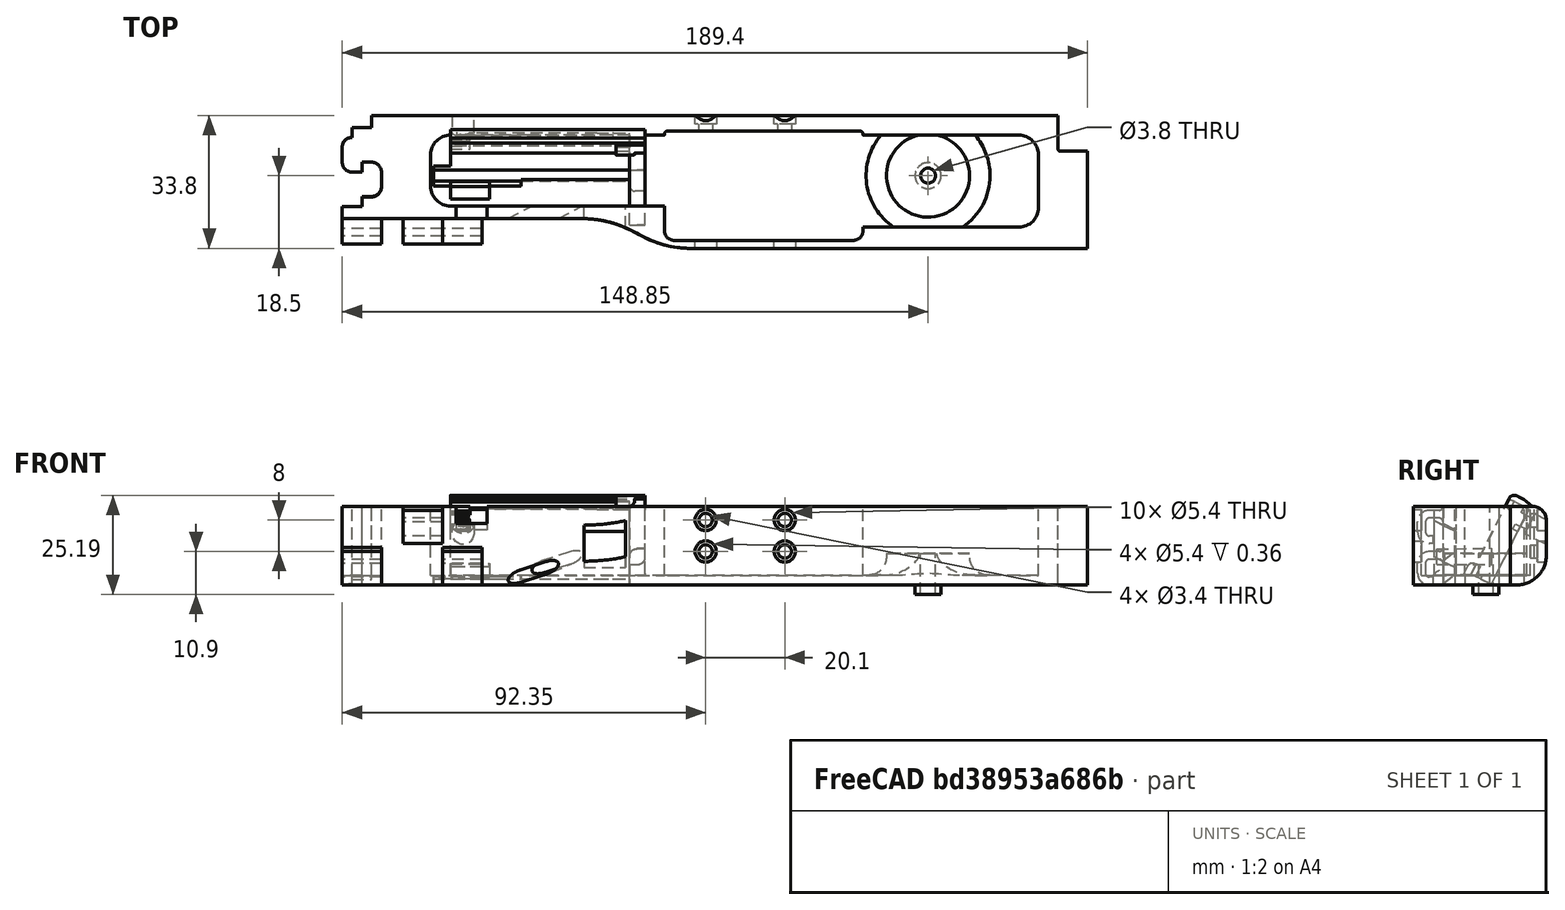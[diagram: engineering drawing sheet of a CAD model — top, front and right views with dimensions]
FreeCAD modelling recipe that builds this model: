
FCSTD DOCUMENT  (FreeCAD 0.19R0.19.2)
Label: v0_9992
License: All rights reserved
LicenseURL: http://en.wikipedia.org/wiki/All_rights_reserved
objects: Sketcher::SketchObject×44, Part::Extrusion×35, Part::MultiFuse×20, Part::Cut×15, Part::Box×14, Part::Fillet×13, App::MeasureDistance×5, Part::Cylinder×4, Part::Revolution×1, Mesh::Feature×1
note: 146 computed .brp shape members not serialized (recipe doc carries the construction recipe); baked Part::Feature solids carry a one-line shape summary decoded from their .brp

FEATURE [Sketcher::SketchObject] Sketch
  FullyConstrained = true
  sketch-geometry (36):
    g0: LineSegment StartX=0 StartY=0 StartZ=0 EndX=154.4 EndY=0 EndZ=0
    g1: LineSegment StartX=154.4 StartY=0 StartZ=0 EndX=154.4 EndY=-7.6 EndZ=0
    g2: LineSegment StartX=32.5209 StartY=-26.2 StartZ=0 EndX=-7.5 EndY=-26.2 EndZ=0
    g3-g7: Circle x5 (B-spline internal-alignment scaffolding for g8; pole/knot coordinates omitted)
    g8: BSplineCurve PolesCount=5 KnotsCount=3 Degree=3 IsPeriodic=0
    g9: GeomPoint X=61.85 Y=-33.8 Z=0
    g10: GeomPoint X=47.185 Y=-29.9 Z=0
    g11: GeomPoint X=32.5209 Y=-26.2 Z=0
    g12: Circle CenterX=121.35 CenterY=-14.3 CenterZ=0 NormalX=0 NormalY=0 NormalZ=1 AngleXU=0 Radius=3.25
    g13: LineSegment StartX=-7.5 StartY=-26.2 StartZ=0 EndX=-27.5 EndY=-26.2 EndZ=0
    g14: LineSegment StartX=-20 StartY=0 StartZ=0 EndX=0 EndY=0 EndZ=0
    g15: LineSegment StartX=-25 StartY=-3.1 StartZ=0 EndX=-20 EndY=-3.1 EndZ=0
    g16: LineSegment StartX=-25 StartY=-3.1 StartZ=0 EndX=-25 EndY=-5.6 EndZ=0
    g17: LineSegment StartX=-27.5 StartY=-8.1 StartZ=0 EndX=-27.5 EndY=-11.85 EndZ=0
    g18: ArcOfCircle CenterX=-25 CenterY=-8.1 CenterZ=0 NormalX=0 NormalY=0 NormalZ=1 AngleXU=0 Radius=2.5 StartAngle=1.5708 EndAngle=3.14159
    g19: LineSegment StartX=-25 StartY=-14.35 StartZ=0 EndX=-22.5 EndY=-14.35 EndZ=0
    g20: ArcOfCircle CenterX=-25 CenterY=-11.85 CenterZ=0 NormalX=0 NormalY=0 NormalZ=1 AngleXU=0 Radius=2.5 StartAngle=3.14159 EndAngle=4.71239
    g21: LineSegment StartX=-22.5 StartY=-14.35 StartZ=0 EndX=-22.5 EndY=-11.85 EndZ=0
    g22: LineSegment StartX=-22.5 StartY=-11.85 StartZ=0 EndX=-20 EndY=-11.85 EndZ=0
    g23: ArcOfCircle CenterX=-20 CenterY=-14.35 CenterZ=0 NormalX=0 NormalY=0 NormalZ=1 AngleXU=0 Radius=2.5 StartAngle=8e-16 EndAngle=1.5708
    g24: LineSegment StartX=-17.5 StartY=-14.35 StartZ=0 EndX=-17.5 EndY=-18.1 EndZ=0
    g25: ArcOfCircle CenterX=-20 CenterY=-18.1 CenterZ=0 NormalX=0 NormalY=0 NormalZ=1 AngleXU=0 Radius=2.5 StartAngle=4.71239 EndAngle=6.28319
    g26: LineSegment StartX=-22.5 StartY=-20.6 StartZ=0 EndX=-20 EndY=-20.6 EndZ=0
    g27: LineSegment StartX=-22.5 StartY=-20.6 StartZ=0 EndX=-22.5 EndY=-23.1 EndZ=0
    g28: LineSegment StartX=-27.5 StartY=-23.1 StartZ=0 EndX=-22.5 EndY=-23.1 EndZ=0
    g29: LineSegment StartX=-20 StartY=-3.1 StartZ=0 EndX=-20 EndY=0 EndZ=0
    g30: LineSegment StartX=-27.5 StartY=-23.1 StartZ=0 EndX=-27.5 EndY=-26.2 EndZ=0
    g31: LineSegment StartX=154.4 StartY=-7.6 StartZ=0 EndX=154.4 EndY=-8.6 EndZ=0
    g32: ArcOfCircle CenterX=154.9 CenterY=-8.6 CenterZ=0 NormalX=0 NormalY=0 NormalZ=1 AngleXU=0 Radius=0.5 StartAngle=3.14159 EndAngle=4.71239
    g33: LineSegment StartX=154.9 StartY=-9.1 StartZ=0 EndX=161.9 EndY=-9.1 EndZ=0
    g34: LineSegment StartX=161.9 StartY=-9.1 StartZ=0 EndX=161.9 EndY=-33.8 EndZ=0
    g35: LineSegment StartX=161.9 StartY=-33.8 StartZ=0 EndX=61.85 EndY=-33.8 EndZ=0
  constraints (72):
    c: PointOnObject(g0,g-2)
    c: Horizontal(g0)
    c: Distance(g0) = 154.4
    c: DistanceY(g-1,g0) = 0
    c: Vertical(g1)
    c: Distance(g1) = 7.6
    c: Coincident(g1,g0)
    c: Horizontal(g2)
    c: Block(g2)
    c: Weight(g3) = 1
    c: Coincident(g8,g2)
    c: InternalAlignment(g3-g7 -> g8) x5
    c: InternalAlignment(g9,g8)
    c: InternalAlignment(g10,g8)
    c: InternalAlignment(g11,g8)
    c: Block(g12)
    c: Coincident(g13,g2)
    c: Horizontal(g13)
    c: Distance(g13) = 20
    c: Horizontal(g14)
    c: Distance(g14) = 20
    c: Coincident(g14,g0)
    c: Horizontal(g15)
    c: Vertical(g16)
    c: Coincident(g16,g15)
    c: Vertical(g17)
    c: Coincident(g18,g16)
    c: Block(g18)
    c: Coincident(g17,g18)
    c: Horizontal(g19)
    c: Coincident(g20,g17)
    c: Block(g20)
    c: Block(g19)
    c: Vertical(g21)
    c: Coincident(g21,g19)
    c: Horizontal(g22)
    c: Coincident(g22,g21)
    c: Coincident(g23,g22)
    c: Vertical(g24)
    c: Block(g23)
    c: Coincident(g24,g23)
    c: Coincident(g25,g24)
    c: Block(g25)
    c: Horizontal(g26)
    c: Coincident(g26,g25)
    c: Vertical(g27)
    c: Coincident(g27,g26)
    c: Horizontal(g28)
    c: Coincident(g28,g27)
    c: Block(g15)
    c: Block(g28)
    c: Coincident(g29,g15)
    c: Coincident(g29,g14)
    c: Vertical(g29)
    c: Coincident(g30,g28)
    c: Coincident(g30,g13)
    c: Vertical(g30)
    c: Vertical(g31)
    c: Distance(g31) = 1
    c: Coincident(g31,g1)
    c: Coincident(g32,g31)
    c: Block(g32)
    c: Coincident(g33,g32)
    c: Horizontal(g33)
    c: Coincident(g34,g33)
    c: Vertical(g34)
    c: Block(g34)
    c: Coincident(g35,g34)
    c: Horizontal(g35)
    c: Block(g35)
    c: Coincident(g8,g35)
    c: Block(g8)
FEATURE [Part::Extrusion] Extrude  label="mainBodyBaseExtrude"
  Base = -> Sketch
  Dir = (0,0,1)
  DirMode = 2
  FaceMakerClass = Part::FaceMakerBullseye
  LengthFwd = 2.4
  LengthRev = 0
  Solid = true
  Symmetric = false
FEATURE [Sketcher::SketchObject] Sketch001
  FullyConstrained = true
  sketch-geometry (75):
    g0: ArcOfCircle CenterX=144.4 CenterY=-10 CenterZ=0 NormalX=0 NormalY=0 NormalZ=1 AngleXU=0 Radius=5 StartAngle=4.345e-13 EndAngle=1.5708
    g1: LineSegment StartX=32.5209 StartY=-26.2 StartZ=0 EndX=-7.49911 EndY=-26.2 EndZ=0
    g2: LineSegment StartX=0 StartY=0 StartZ=0 EndX=154.4 EndY=0 EndZ=0
    g3-g7: Circle x5 (B-spline internal-alignment scaffolding for g8; pole/knot coordinates omitted)
    g8: BSplineCurve PolesCount=5 KnotsCount=3 Degree=3 IsPeriodic=0
    g9: GeomPoint X=61.85 Y=-33.8 Z=0
    g10: GeomPoint X=47.1857 Y=-29.9 Z=0
    g11: GeomPoint X=32.5209 Y=-26.2 Z=0
    g12: LineSegment StartX=154.4 StartY=0 StartZ=0 EndX=154.4 EndY=-7.6 EndZ=0
    g13: LineSegment StartX=20 StartY=-5 StartZ=0 EndX=54.35 EndY=-5 EndZ=0
    g14: LineSegment StartX=104.85 StartY=-5 StartZ=0 EndX=144.4 EndY=-5 EndZ=0
    g15: LineSegment StartX=54.35 StartY=-23 StartZ=0 EndX=20 EndY=-23 EndZ=0
    g16: LineSegment StartX=-27.4991 StartY=-26.2 StartZ=0 EndX=-7.49911 EndY=-26.2 EndZ=0
    g17: LineSegment StartX=-20 StartY=0 StartZ=0 EndX=0 EndY=0 EndZ=0
    g18: LineSegment StartX=-27.4991 StartY=-23.2 StartZ=0 EndX=-22.5 EndY=-23.2 EndZ=0
    g19: LineSegment StartX=-22.5 StartY=-20.7 StartZ=0 EndX=-22.5 EndY=-23.2 EndZ=0
    g20: LineSegment StartX=-22.5 StartY=-20.7 StartZ=0 EndX=-20 EndY=-20.7 EndZ=0
    g21: ArcOfCircle CenterX=-20 CenterY=-18.2 CenterZ=0 NormalX=0 NormalY=0 NormalZ=1 AngleXU=0 Radius=2.5 StartAngle=4.71239 EndAngle=6.28319
    g22: LineSegment StartX=-17.5 StartY=-14.4 StartZ=0 EndX=-17.5 EndY=-18.2 EndZ=0
    g23: ArcOfCircle CenterX=-20 CenterY=-14.4 CenterZ=0 NormalX=0 NormalY=0 NormalZ=1 AngleXU=0 Radius=2.5 StartAngle=9e-16 EndAngle=1.5708
    g24: LineSegment StartX=-22.5 StartY=-11.9 StartZ=0 EndX=-20 EndY=-11.9 EndZ=0
    g25: LineSegment StartX=-22.5 StartY=-14.4 StartZ=0 EndX=-22.5 EndY=-11.9 EndZ=0
    g26: LineSegment StartX=-25 StartY=-14.4 StartZ=0 EndX=-22.5 EndY=-14.4 EndZ=0
    g27: ArcOfCircle CenterX=-25 CenterY=-11.9 CenterZ=0 NormalX=0 NormalY=0 NormalZ=1 AngleXU=0 Radius=2.5 StartAngle=3.14159 EndAngle=4.71239
    g28: LineSegment StartX=-27.5 StartY=-8.1 StartZ=0 EndX=-27.5 EndY=-11.9 EndZ=0
    g29: ArcOfCircle CenterX=-25 CenterY=-8.1 CenterZ=0 NormalX=0 NormalY=0 NormalZ=1 AngleXU=0 Radius=2.5 StartAngle=1.5708 EndAngle=3.14159
    g30: LineSegment StartX=-25 StartY=-3.1 StartZ=0 EndX=-25 EndY=-5.6 EndZ=0
    g31: LineSegment StartX=-20 StartY=-3.1 StartZ=0 EndX=-25 EndY=-3.1 EndZ=0
    g32: LineSegment StartX=-20 StartY=0 StartZ=0 EndX=-20 EndY=-3.1 EndZ=0
    g33: LineSegment StartX=-27.4991 StartY=-26.2 StartZ=0 EndX=-27.4991 EndY=-23.2 EndZ=0
    g34: LineSegment StartX=4.09e-14 StartY=-5 StartZ=0 EndX=20 EndY=-5 EndZ=0
    g35: ArcOfCircle CenterX=7.1e-15 CenterY=-18 CenterZ=0 NormalX=0 NormalY=0 NormalZ=1 AngleXU=0 Radius=5 StartAngle=3.14159 EndAngle=4.71239
    g36: ArcOfCircle CenterX=4.26e-14 CenterY=-10 CenterZ=0 NormalX=0 NormalY=0 NormalZ=1 AngleXU=0 Radius=5 StartAngle=1.5708 EndAngle=3.14159
    g37: LineSegment StartX=-5 StartY=-18 StartZ=0 EndX=-5 EndY=-10 EndZ=0
    g38: LineSegment StartX=6.2e-15 StartY=-23 StartZ=0 EndX=20 EndY=-23 EndZ=0
    g39: LineSegment StartX=154.4 StartY=-7.6 StartZ=0 EndX=154.4 EndY=-8.6 EndZ=0
    g40: LineSegment StartX=154.9 StartY=-9.1 StartZ=0 EndX=161.9 EndY=-9.1 EndZ=0
    g41: ArcOfCircle CenterX=154.9 CenterY=-8.6 CenterZ=0 NormalX=0 NormalY=0 NormalZ=1 AngleXU=0 Radius=0.5 StartAngle=3.14159 EndAngle=4.71299
    g42: LineSegment StartX=104.85 StartY=-28.3916 StartZ=0 EndX=144.408 EndY=-28.3916 EndZ=0
    g43: LineSegment StartX=149.4 StartY=-10 StartZ=0 EndX=149.4 EndY=-23.4 EndZ=0
    g44: ArcOfCircle CenterX=144.408 CenterY=-23.4 CenterZ=0 NormalX=0 NormalY=0 NormalZ=1 AngleXU=0 Radius=4.99164 StartAngle=4.71239 EndAngle=6.28319
    g45: LineSegment StartX=104.85 StartY=-28.3916 StartZ=0 EndX=104.85 EndY=-28.7833 EndZ=0
    g46: LineSegment StartX=54.35 StartY=-28.7916 StartZ=0 EndX=54.35 EndY=-23 EndZ=0
    g47: LineSegment StartX=161.9 StartY=-33.8 StartZ=0 EndX=161.9 EndY=-9.1 EndZ=0
    g48: LineSegment StartX=61.85 StartY=-33.8 StartZ=0 EndX=161.9 EndY=-33.8 EndZ=0
    g49: Circle CenterX=54.35 CenterY=-28.7916 CenterZ=0 NormalX=0 NormalY=0 NormalZ=1 AngleXU=0 Radius=1
    g50: Circle CenterX=54.35 CenterY=-31.7916 CenterZ=0 NormalX=0 NormalY=0 NormalZ=1 AngleXU=0 Radius=1
    g51: Circle CenterX=57.35 CenterY=-31.7916 CenterZ=0 NormalX=0 NormalY=0 NormalZ=1 AngleXU=0 Radius=1
    g52: BSplineCurve PolesCount=3 KnotsCount=2 Degree=2 IsPeriodic=0
    g53: GeomPoint X=54.35 Y=-28.7916 Z=0
    g54: GeomPoint X=57.35 Y=-31.7916 Z=0
    g55: Circle CenterX=104.85 CenterY=-28.7833 CenterZ=0 NormalX=0 NormalY=0 NormalZ=1 AngleXU=0 Radius=1
    g56: Circle CenterX=104.85 CenterY=-31.7916 CenterZ=0 NormalX=0 NormalY=0 NormalZ=1 AngleXU=0 Radius=1
    g57: Circle CenterX=101.85 CenterY=-31.7916 CenterZ=0 NormalX=0 NormalY=0 NormalZ=1 AngleXU=0 Radius=1
    g58: BSplineCurve PolesCount=3 KnotsCount=2 Degree=2 IsPeriodic=0
    g59: GeomPoint X=104.85 Y=-28.7833 Z=0
    g60: GeomPoint X=101.85 Y=-31.7916 Z=0
    g61: LineSegment StartX=57.35 StartY=-31.7916 StartZ=0 EndX=101.85 EndY=-31.7916 EndZ=0
    g62: Circle CenterX=54.35 CenterY=-5 CenterZ=0 NormalX=0 NormalY=0 NormalZ=1 AngleXU=0 Radius=1
    g63: Circle CenterX=54.35 CenterY=-4 CenterZ=0 NormalX=0 NormalY=0 NormalZ=1 AngleXU=0 Radius=1
    g64: Circle CenterX=55.15 CenterY=-4 CenterZ=0 NormalX=0 NormalY=0 NormalZ=1 AngleXU=0 Radius=1
    g65: BSplineCurve PolesCount=3 KnotsCount=2 Degree=2 IsPeriodic=0
    g66: GeomPoint X=54.35 Y=-5 Z=0
    g67: GeomPoint X=55.15 Y=-4 Z=0
    g68: Circle CenterX=104.85 CenterY=-5 CenterZ=0 NormalX=0 NormalY=0 NormalZ=1 AngleXU=0 Radius=1
    g69: Circle CenterX=104.85 CenterY=-4 CenterZ=0 NormalX=0 NormalY=0 NormalZ=1 AngleXU=0 Radius=1
    g70: Circle CenterX=104.05 CenterY=-4 CenterZ=0 NormalX=0 NormalY=0 NormalZ=1 AngleXU=0 Radius=1
    g71: BSplineCurve PolesCount=3 KnotsCount=2 Degree=2 IsPeriodic=0
    g72: GeomPoint X=104.85 Y=-5 Z=0
    g73: GeomPoint X=104.05 Y=-4 Z=0
    g74: LineSegment StartX=104.05 StartY=-4 StartZ=0 EndX=55.15 EndY=-4 EndZ=0
  constraints (156):
    c: PointOnObject(g2,g-2)
    c: DistanceY(g-1,g2) = 0
    c: Block(g0)
    c: Horizontal(g1)
    c: Distance(g1) = 40.02
    c: Horizontal(g2)
    c: Block(g2)
    c: Weight(g3) = 1
    c: Equal(g3, g4-g7) x4
    c: Coincident(g8,g1)
    c: InternalAlignment(g3-g7 -> g8) x5
    c: InternalAlignment(g9,g8)
    c: InternalAlignment(g10,g8)
    c: InternalAlignment(g11,g8)
    c: Vertical(g12)
    c: Coincident(g12,g2)
    c: Distance(g12) = 7.6
    c: Block(g12)
    c: Horizontal(g13)
    c: Coincident(g14,g0)
    c: Horizontal(g14)
    c: Horizontal(g15)
    c: Horizontal(g16)
    c: Distance(g16) = 20
    c: Coincident(g1,g16)
    c: Horizontal(g17)
    c: Distance(g17) = 20
    c: Coincident(g17,g2)
    c: Horizontal(g31)
    c: Vertical(g30)
    c: Coincident(g29,g30)
    c: Vertical(g28)
    c: Block(g29)
    c: Coincident(g27,g28)
    c: Block(g27)
    c: Horizontal(g26)
    c: Coincident(g26,g27)
    c: Vertical(g25)
    c: Coincident(g25,g26)
    c: Horizontal(g24)
    c: Coincident(g23,g24)
    c: Block(g23)
    c: Vertical(g22)
    c: Coincident(g21,g22)
    c: Block(g21)
    c: Horizontal(g20)
    c: Coincident(g20,g21)
    c: Vertical(g19)
    c: Coincident(g19,g20)
    c: Horizontal(g18)
    c: Coincident(g18,g19)
    c: Coincident(g32,g17)
    c: Coincident(g32,g31)
    c: Vertical(g32)
    c: Coincident(g33,g16)
    c: Coincident(g33,g18)
    c: Vertical(g33)
    c: Block(g33)
    c: Block(g18)
    c: Block(g22)
    c: Block(g26)
    c: Block(g25)
    c: Block(g24)
    c: Block(g28)
    c: Block(g31)
    c: Block(g30)
    c: Horizontal(g34)
    c: Distance(g34) = 20
    c: Block(g35)
    c: Block(g36)
    c: Coincident(g37,g35)
    c: Coincident(g37,g36)
    c: Vertical(g37)
    c: Coincident(g38,g35)
    c: Coincident(g38,g15)
    c: Horizontal(g38)
    c: Block(g38)
    c: Block(g34)
    c: Block(g13)
    c: Vertical(g39)
    c: Distance(g39) = 1
    c: Coincident(g39,g12)
    c: Horizontal(g40)
    c: Coincident(g41,g39)
    c: Coincident(g41,g40)
    c: Block(g39)
    c: Block(g41)
    c: Horizontal(g42)
    c: Vertical(g43)
    c: Distance(g43) = 13.4
    c: Coincident(g43,g0)
    c: Block(g42)
    c: Block(g43)
    c: Coincident(g44,g43)
    c: Coincident(g44,g42)
    c: Block(g44)
    c: Distance(g15) = 34.35
    c: Coincident(g45,g42)
    c: Vertical(g45)
    c: Coincident(g46,g15)
    c: Vertical(g46)
    c: Coincident(g47,g40)
    c: Vertical(g47)
    c: Block(g47)
    c: Coincident(g48,g47)
    c: Horizontal(g48)
    c: Block(g48)
    c: Coincident(g8,g48)
    c: Block(g8)
    c: Coincident(g52,g46)
    c: Weight(g49) = 1
    c: Equal(g49,g50)
    c: Equal(g49,g51)
    c: InternalAlignment(g49,g52)
    c: InternalAlignment(g50,g52)
    c: InternalAlignment(g51,g52)
    c: InternalAlignment(g53,g52)
    c: InternalAlignment(g54,g52)
    c: Coincident(g58,g45)
    c: Weight(g55) = 1
    c: Equal(g55,g56)
    c: Equal(g55,g57)
    c: InternalAlignment(g55,g58)
    c: InternalAlignment(g56,g58)
    c: InternalAlignment(g57,g58)
    c: InternalAlignment(g59,g58)
    c: InternalAlignment(g60,g58)
    c: Block(g58)
    c: Block(g52)
    c: Coincident(g61,g52)
    c: Coincident(g61,g58)
    c: Horizontal(g61)
    c: Block(g14)
    c: Coincident(g65,g13)
    c: Weight(g62) = 1
    c: Equal(g62,g63)
    c: Equal(g62,g64)
    c: InternalAlignment(g62,g65)
    c: InternalAlignment(g63,g65)
    c: InternalAlignment(g64,g65)
    c: InternalAlignment(g66,g65)
    c: InternalAlignment(g67,g65)
    c: Block(g65)
    c: Coincident(g71,g14)
    c: Weight(g68) = 1
    c: Equal(g68,g69)
    c: Equal(g68,g70)
    c: InternalAlignment(g68,g71)
    c: InternalAlignment(g69,g71)
    c: InternalAlignment(g70,g71)
    c: InternalAlignment(g72,g71)
    c: InternalAlignment(g73,g71)
    c: Block(g71)
    c: Coincident(g74,g71)
    c: Coincident(g74,g65)
    c: Horizontal(g74)
FEATURE [Sketcher::SketchObject] Sketch005
  FullyConstrained = true
  Placement = pos=(0,0,0) rot=(1,0,0;1.5708rad)
  sketch-geometry (4):
    g0: Circle CenterX=84.95 CenterY=16.5 CenterZ=0 NormalX=0 NormalY=0 NormalZ=1 AngleXU=0 Radius=1.7
    g1: Circle CenterX=84.95 CenterY=8.5 CenterZ=0 NormalX=0 NormalY=0 NormalZ=1 AngleXU=0 Radius=1.7
    g2: Circle CenterX=64.85 CenterY=8.5 CenterZ=0 NormalX=0 NormalY=0 NormalZ=1 AngleXU=0 Radius=1.7
    g3: Circle CenterX=64.85 CenterY=16.5 CenterZ=0 NormalX=0 NormalY=0 NormalZ=1 AngleXU=0 Radius=1.7
  constraints (4):
    c: Block(g0)
    c: Block(g1)
    c: Block(g2)
    c: Block(g3)
FEATURE [Part::Extrusion] Extrude004  label="removeFromMainBodyToCreateScrewHolesForSolenoidExtrude004"
  Base = -> Sketch005
  Dir = (0,-1,1.1e-15)
  DirMode = 2
  FaceMakerClass = Part::FaceMakerBullseye
  LengthFwd = 10
  LengthRev = 0
  Solid = true
  Symmetric = false
FEATURE [Sketcher::SketchObject] Sketch004
  FullyConstrained = true
  Placement = pos=(0,0,0) rot=(1,0,0;1.5708rad)
  sketch-geometry (12):
    g0: LineSegment StartX=15.75 StartY=2.5 StartZ=0 EndX=15.75 EndY=0 EndZ=0
    g1: Circle CenterX=15.75 CenterY=2.5 CenterZ=0 NormalX=0 NormalY=0 NormalZ=1 AngleXU=0 Radius=1
    g2: Circle CenterX=10.55 CenterY=2.5 CenterZ=0 NormalX=0 NormalY=0 NormalZ=1 AngleXU=0 Radius=1
    g3: Circle CenterX=10.55 CenterY=8 CenterZ=0 NormalX=0 NormalY=0 NormalZ=1 AngleXU=0 Radius=1
    g4: BSplineCurve PolesCount=3 KnotsCount=2 Degree=2 IsPeriodic=0
    g5: GeomPoint X=15.75 Y=2.5 Z=0
    g6: GeomPoint X=10.55 Y=8 Z=0
    g7: LineSegment StartX=1.9 StartY=8 StartZ=0 EndX=10.55 EndY=8 EndZ=0
    g8: LineSegment StartX=1.9 StartY=-2.4 StartZ=0 EndX=1.9 EndY=8 EndZ=0
    g9: LineSegment StartX=3.30092 StartY=-2.4 StartZ=0 EndX=3.30092 EndY=0 EndZ=0
    g10: LineSegment StartX=15.75 StartY=0 StartZ=0 EndX=3.30092 EndY=0 EndZ=0
    g11: LineSegment StartX=3.30092 StartY=-2.4 StartZ=0 EndX=1.9 EndY=-2.4 EndZ=0
  constraints (26):
    c: Vertical(g0)
    c: Distance(g0) = 2.5
    c: Coincident(g4,g0)
    c: Weight(g1) = 1
    c: Equal(g1,g2)
    c: Equal(g1,g3)
    c: InternalAlignment(g1,g4)
    c: InternalAlignment(g2,g4)
    c: InternalAlignment(g3,g4)
    c: InternalAlignment(g5,g4)
    c: InternalAlignment(g6,g4)
    c: Block(g4)
    c: Coincident(g7,g4)
    c: Horizontal(g7)
    c: Vertical(g8)
    c: Coincident(g8,g7)
    c: Block(g8)
    c: Vertical(g9)
    c: Coincident(g10,g0)
    c: PointOnObject(g10,g-1)
    c: Horizontal(g10)
    c: Coincident(g10,g9)
    c: Block(g9)
    c: Coincident(g11,g9)
    c: Coincident(g11,g8)
    c: Horizontal(g11)
FEATURE [Sketcher::SketchObject] Sketch007
  FullyConstrained = true
  Placement = pos=(0,-14.3,2.37) rot=(-1,0,0;2.03453rad)
  sketch-geometry (6):
    g0: LineSegment StartX=0 StartY=0 StartZ=0 EndX=45.5 EndY=0 EndZ=0
    g1: LineSegment StartX=0 StartY=0 StartZ=0 EndX=0 EndY=-21.2 EndZ=0
    g2: LineSegment StartX=45.5 StartY=0 StartZ=0 EndX=49.5 EndY=0 EndZ=0
    g3: LineSegment StartX=49.5 StartY=0 StartZ=0 EndX=49.5 EndY=-21.2 EndZ=0
    g4: LineSegment StartX=49.5 StartY=-21.2 StartZ=0 EndX=0 EndY=-21.2 EndZ=0
    g5: Circle CenterX=3.25 CenterY=-18.05 CenterZ=0 NormalX=0 NormalY=0 NormalZ=1 AngleXU=0 Radius=1.6
  constraints (15):
    c: Coincident(g0,g-1)
    c: Horizontal(g0)
    c: Distance(g0) = 45.5
    c: Coincident(g1,g0)
    c: Vertical(g1)
    c: Horizontal(g2)
    c: Distance(g2) = 4
    c: Coincident(g2,g0)
    c: Coincident(g3,g2)
    c: Vertical(g3)
    c: Block(g3)
    c: Coincident(g4,g3)
    c: Horizontal(g4)
    c: Coincident(g4,g1)
    c: Block(g5)
FEATURE [Part::Extrusion] Extrude005  label="solenoidDriverHolderExtrude005"
  Base = -> Sketch007
  Dir = (0,0.894389,-0.447291)
  DirMode = 2
  FaceMakerClass = Part::FaceMakerBullseye
  LengthFwd = 10
  LengthRev = 0
  Placement = pos=(0,0,-2) rot=(0,0,1;0rad)
  Solid = true
  Symmetric = false
FEATURE [Sketcher::SketchObject] Sketch008
  FullyConstrained = false
  Placement = pos=(0,-4.3,-2.6) rot=(-1,0,0;2.03453rad)
  sketch-geometry (1):
    g0: Circle CenterX=42.25 CenterY=-3.15 CenterZ=0 NormalX=0 NormalY=0 NormalZ=1 AngleXU=0 Radius=4.5
FEATURE [Sketcher::SketchObject] Sketch009
  FullyConstrained = true
  Placement = pos=(0,-4.3,-2.6) rot=(-1,0,0;2.03453rad)
  sketch-geometry (1):
    g0: Circle CenterX=3.25 CenterY=-18.0217 CenterZ=0 NormalX=0 NormalY=0 NormalZ=1 AngleXU=0 Radius=2.8
  constraints (1):
    c: Block(g0)
FEATURE [Sketcher::SketchObject] Sketch010
  FullyConstrained = true
  Placement = pos=(0,-14.3,2.37) rot=(-1,0,0;2.03453rad)
  sketch-geometry (1):
    g0: Circle CenterX=3.25 CenterY=-18.05 CenterZ=0 NormalX=0 NormalY=0 NormalZ=1 AngleXU=0 Radius=1.6
  constraints (1):
    c: Block(g0)
FEATURE [Part::Extrusion] Extrude008  label="removeFromScrewHole3"
  Base = -> Sketch010
  Dir = (0,0.894389,-0.447291)
  DirMode = 2
  FaceMakerClass = Part::FaceMakerBullseye
  LengthFwd = -25
  LengthRev = 0
  Placement = pos=(0,4,-4) rot=(0,0,1;0rad)
  Solid = true
  Symmetric = false
FEATURE [Sketcher::SketchObject] Sketch011
  FullyConstrained = true
  Placement = pos=(0,-14.3,2.37) rot=(-1,0,0;2.03453rad)
  sketch-geometry (4):
    g0: LineSegment StartX=49.5 StartY=-21.2 StartZ=0 EndX=49.5 EndY=-22.8 EndZ=0
    g1: LineSegment StartX=49.5 StartY=-22.8 StartZ=0 EndX=0.002238 EndY=-22.8 EndZ=0
    g2: LineSegment StartX=0.002238 StartY=-21.2 StartZ=0 EndX=0.002238 EndY=-22.8 EndZ=0
    g3: LineSegment StartX=49.5 StartY=-21.2 StartZ=0 EndX=0.002238 EndY=-21.2 EndZ=0
  constraints (10):
    c: Vertical(g0)
    c: Distance(g0) = 1.6
    c: Coincident(g1,g0)
    c: Horizontal(g1)
    c: Vertical(g2)
    c: Coincident(g2,g1)
    c: Coincident(g3,g0)
    c: Coincident(g3,g2)
    c: Horizontal(g3)
    c: Block(g3)
FEATURE [Part::Extrusion] Extrude009  label="solenoidDriverTopLipFront"
  Base = -> Sketch011
  Dir = (0,0.894389,-0.447291)
  DirMode = 2
  FaceMakerClass = Part::FaceMakerBullseye
  LengthFwd = -2
  LengthRev = 0
  Placement = pos=(0,-2.9,-0.35) rot=(0,0,1;0rad)
  Solid = true
  Symmetric = false
FEATURE [Sketcher::SketchObject] Sketch012
  FullyConstrained = true
  Placement = pos=(0,-14.3,2.37) rot=(-1,0,0;2.03453rad)
  sketch-geometry (4):
    g0: LineSegment StartX=49.5 StartY=-21.2 StartZ=0 EndX=49.5 EndY=-22.8 EndZ=0
    g1: LineSegment StartX=49.5 StartY=-22.8 StartZ=0 EndX=0.002238 EndY=-22.8 EndZ=0
    g2: LineSegment StartX=0.002238 StartY=-21.2 StartZ=0 EndX=0.002238 EndY=-22.8 EndZ=0
    g3: LineSegment StartX=49.5 StartY=-21.2 StartZ=0 EndX=0.002238 EndY=-21.2 EndZ=0
  constraints (10):
    c: Vertical(g0)
    c: Distance(g0) = 1.6
    c: Coincident(g1,g0)
    c: Horizontal(g1)
    c: Vertical(g2)
    c: Coincident(g2,g1)
    c: Coincident(g3,g0)
    c: Coincident(g3,g2)
    c: Horizontal(g3)
    c: Block(g3)
FEATURE [Part::Extrusion] Extrude010  label="solenoidDriverTopLipLowerExtrude010"
  Base = -> Sketch012
  Dir = (0,0.894389,-0.447291)
  DirMode = 2
  FaceMakerClass = Part::FaceMakerBullseye
  LengthFwd = 5.05
  LengthRev = 0
  Solid = true
  Symmetric = false
FEATURE [Sketcher::SketchObject] Sketch015
  FullyConstrained = true
  Placement = pos=(0,-14.3,2.37) rot=(-1,0,0;2.03453rad)
  sketch-geometry (4):
    g0: LineSegment StartX=0 StartY=1.5 StartZ=0 EndX=0 EndY=0 EndZ=0
    g1: LineSegment StartX=0 StartY=1.5 StartZ=0 EndX=5 EndY=1.5 EndZ=0
    g2: LineSegment StartX=5 StartY=1.5 StartZ=0 EndX=5 EndY=0 EndZ=0
    g3: LineSegment StartX=0 StartY=0 StartZ=0 EndX=5 EndY=0 EndZ=0
  constraints (13):
    c: Vertical(g0)
    c: Distance(g0) = 1.5
    c: Horizontal(g1)
    c: Distance(g1) = 5
    c: Coincident(g1,g0)
    c: Vertical(g2)
    c: Distance(g2) = 1.5
    c: Coincident(g2,g1)
    c: Block(g1)
    c: Block(g2)
    c: Block(g0)
    c: Coincident(g3,g0)
    c: Coincident(g3,g2)
FEATURE [Part::Extrusion] Extrude013  label="solenoidDriverBottomLipTopExtrude012"
  Base = -> Sketch015
  Dir = (0,0.894389,-0.447291)
  DirMode = 2
  FaceMakerClass = Part::FaceMakerBullseye
  LengthFwd = -6.5
  LengthRev = 0
  Placement = pos=(0,-14.15,19.65) rot=(1,0,0;1.5708rad)
  Solid = true
  Symmetric = false
FEATURE [Sketcher::SketchObject] Sketch016
  FullyConstrained = true
  Placement = pos=(0,0,0) rot=(1,0,0;1.5708rad)
  sketch-geometry (4):
    g0: Circle CenterX=84.15 CenterY=16.5 CenterZ=0 NormalX=0 NormalY=0 NormalZ=1 AngleXU=0 Radius=2.7
    g1: Circle CenterX=64.05 CenterY=16.5 CenterZ=0 NormalX=0 NormalY=0 NormalZ=1 AngleXU=0 Radius=2.7
    g2: Circle CenterX=64.05 CenterY=8.5 CenterZ=0 NormalX=0 NormalY=0 NormalZ=1 AngleXU=0 Radius=2.7
    g3: Circle CenterX=84.15 CenterY=8.5 CenterZ=0 NormalX=0 NormalY=0 NormalZ=1 AngleXU=0 Radius=2.7
  constraints (4):
    c: Block(g0)
    c: Block(g1)
    c: Block(g3)
    c: Block(g2)
FEATURE [Part::Extrusion] Extrude014  label="removeFromMainBodyToCreateScrewHoleCounterSinks"
  Base = -> Sketch016
  Dir = (0,-1,1.1e-15)
  DirMode = 2
  FaceMakerClass = Part::FaceMakerBullseye
  LengthFwd = 1.9
  LengthRev = 0
  Placement = pos=(0.8,-0.36,0) rot=(0,0,1;0rad)
  Solid = true
  Symmetric = false
FEATURE [Part::Extrusion] Extrude015  label="removeFromScrewHole2Extrude007"
  Base = -> Sketch009
  Dir = (0,0.894389,-0.447291)
  DirMode = 2
  FaceMakerClass = Part::FaceMakerBullseye
  LengthFwd = 10
  LengthRev = 0
  Placement = pos=(0,-8,2) rot=(0,0,1;0rad)
  Solid = true
  Symmetric = false
FEATURE [Sketcher::SketchObject] Sketch017
  FullyConstrained = true
  Placement = pos=(0,-14.3,2.37) rot=(-1,0,0;2.03453rad)
  sketch-geometry (4):
    g0: LineSegment StartX=0 StartY=1.5 StartZ=0 EndX=0 EndY=0 EndZ=0
    g1: LineSegment StartX=0 StartY=1.5 StartZ=0 EndX=5 EndY=1.5 EndZ=0
    g2: LineSegment StartX=5 StartY=1.5 StartZ=0 EndX=5 EndY=0 EndZ=0
    g3: LineSegment StartX=0 StartY=0 StartZ=0 EndX=5 EndY=0 EndZ=0
  constraints (13):
    c: Vertical(g0)
    c: Distance(g0) = 1.5
    c: Horizontal(g1)
    c: Distance(g1) = 5
    c: Coincident(g1,g0)
    c: Vertical(g2)
    c: Distance(g2) = 1.5
    c: Coincident(g2,g1)
    c: Block(g1)
    c: Block(g2)
    c: Block(g0)
    c: Coincident(g3,g0)
    c: Coincident(g3,g2)
FEATURE [Part::Extrusion] Extrude016  label="solenoidDriverBottomLipTopExtrude013"
  Base = -> Sketch017
  Dir = (0,0.894389,-0.447291)
  DirMode = 2
  FaceMakerClass = Part::FaceMakerBullseye
  LengthFwd = -6.5
  LengthRev = 0
  Placement = pos=(0,-15.45,20.3) rot=(1,0,0;1.5708rad)
  Solid = true
  Symmetric = false
FEATURE [Part::Fillet] Fillet005  label="solenoidDriverBottomLipTopFillet005"
  Base = -> Extrude016
  Edges = 1 edges r=1.4: [Edge6]
FEATURE [Sketcher::SketchObject] Sketch018
  FullyConstrained = true
  Placement = pos=(38.5,-14.3,2.37) rot=(-1,0,0;2.03453rad)
  sketch-geometry (4):
    g0: LineSegment StartX=11 StartY=0 StartZ=0 EndX=11 EndY=1.5 EndZ=0
    g1: LineSegment StartX=11 StartY=0 StartZ=0 EndX=3.6 EndY=0 EndZ=0
    g2: LineSegment StartX=3.6 StartY=0 StartZ=0 EndX=3.6 EndY=1.5 EndZ=0
    g3: LineSegment StartX=11 StartY=1.5 StartZ=0 EndX=3.6 EndY=1.5 EndZ=0
  constraints (12):
    c: PointOnObject(g0,g-1)
    c: Vertical(g0)
    c: Distance(g0) = 1.5
    c: Horizontal(g1)
    c: Distance(g1) = 7.4
    c: Coincident(g1,g0)
    c: Block(g0)
    c: Coincident(g2,g1)
    c: Vertical(g2)
    c: Coincident(g3,g0)
    c: Horizontal(g3)
    c: Coincident(g2,g3)
FEATURE [Part::Extrusion] Extrude017
  Base = -> Sketch018
  Dir = (0,0.894389,-0.447291)
  DirMode = 2
  FaceMakerClass = Part::FaceMakerBullseye
  LengthFwd = 4
  LengthRev = 0
  Placement = pos=(0,-8.212,34.025) rot=(1,0,0;1.5708rad)
  Solid = true
  Symmetric = false
FEATURE [Sketcher::SketchObject] Sketch019
  FullyConstrained = true
  Placement = pos=(0,0,0) rot=(1,0,0;1.5708rad)
  sketch-geometry (4):
    g0: Circle CenterX=84.95 CenterY=8.5 CenterZ=0 NormalX=0 NormalY=0 NormalZ=1 AngleXU=0 Radius=2.7
    g1: Circle CenterX=64.85 CenterY=8.5 CenterZ=0 NormalX=0 NormalY=0 NormalZ=1 AngleXU=0 Radius=2.7
    g2: Circle CenterX=64.85 CenterY=16.5 CenterZ=0 NormalX=0 NormalY=0 NormalZ=1 AngleXU=0 Radius=2.7
    g3: Circle CenterX=84.95 CenterY=16.5 CenterZ=0 NormalX=0 NormalY=0 NormalZ=1 AngleXU=0 Radius=2.7
  constraints (4):
    c: Block(g3)
    c: Block(g2)
    c: Block(g0)
    c: Block(g1)
FEATURE [Part::Extrusion] Extrude019  label="removeSolenoidAdjusterHoles"
  Base = -> Sketch019
  Dir = (0,-1,1.1e-15)
  DirMode = 2
  FaceMakerClass = Part::FaceMakerBullseye
  LengthFwd = 6
  LengthRev = 0
  Placement = pos=(0,-30,0) rot=(0,0,1;0rad)
  Solid = true
  Symmetric = false
FEATURE [Sketcher::SketchObject] Sketch020
  FullyConstrained = true
  Placement = pos=(0,-14.3,2.37) rot=(-1,0,0;2.03453rad)
  sketch-geometry (6):
    g0: LineSegment StartX=45.5 StartY=-21.2 StartZ=0 EndX=49.5 EndY=-21.2 EndZ=0
    g1: LineSegment StartX=45.5 StartY=0 StartZ=0 EndX=49.5 EndY=0 EndZ=0
    g2: LineSegment StartX=49.5 StartY=0 StartZ=0 EndX=49.5 EndY=-21.2 EndZ=0
    g3: LineSegment StartX=4 StartY=0 StartZ=0 EndX=4 EndY=-21.2 EndZ=0
    g4: LineSegment StartX=45.5 StartY=-21.2 StartZ=0 EndX=4 EndY=-21.2 EndZ=0
    g5: LineSegment StartX=4 StartY=0 StartZ=0 EndX=45.5 EndY=0 EndZ=0
  constraints (16):
    c: Horizontal(g0)
    c: Distance(g0) = 4
    c: Horizontal(g1)
    c: Distance(g1) = 4
    c: Coincident(g2,g1)
    c: Coincident(g2,g0)
    c: Vertical(g2)
    c: Block(g2)
    c: Vertical(g3)
    c: Coincident(g4,g0)
    c: Horizontal(g4)
    c: Coincident(g4,g3)
    c: Coincident(g5,g1)
    c: Horizontal(g5)
    c: Block(g3)
    c: Block(g5)
FEATURE [Part::Box] Box  label="Cube"
  AttacherType = Attacher::AttachEngine3D
  Height = 10
  Length = 190
  Placement = pos=(-30,0,0) rot=(0,0,1;0rad)
  Width = 10
FEATURE [Part::Fillet] Fillet008
  Base = -> Box
  Edges = 1 edges r=7.5: [Edge11]
FEATURE [Part::Box] Box001  label="Cube001"
  AttacherType = Attacher::AttachEngine3D
  Height = 10
  Length = 190
  Placement = pos=(-35,0,0) rot=(0,0,1;0rad)
  Width = 10
FEATURE [Part::Cut] Cut  label="filletMain"
  Base = -> Box001
  Placement = pos=(0,-10,0) rot=(0,0,1;0rad)
  Tool = -> Fillet008
FEATURE [Part::Box] Box002  label="Cube002"
  AttacherType = Attacher::AttachEngine3D
  Height = 30
  Length = 190
  Placement = pos=(-20,0,0) rot=(0,0,1;0rad)
  Width = 10
FEATURE [Part::Box] Box003  label="Cube003"
  AttacherType = Attacher::AttachEngine3D
  Height = 10
  Length = 190
  Placement = pos=(-90,-50,-10) rot=(0,0,1;0rad)
  Width = 50
FEATURE [Sketcher::SketchObject] Sketch021
  FullyConstrained = true
  Placement = pos=(0,-14.3,2.37) rot=(-1,0,0;2.03453rad)
  sketch-geometry (6):
    g0: LineSegment StartX=41.65 StartY=-3.15 StartZ=0 EndX=38.95 EndY=-3.15 EndZ=0
    g1: LineSegment StartX=36.25 StartY=-3.15 StartZ=0 EndX=38.95 EndY=-3.15 EndZ=0
    g2: LineSegment StartX=41.65 StartY=-3.15 StartZ=0 EndX=41.65 EndY=-7.15 EndZ=0
    g3: LineSegment StartX=38.95 StartY=-7.15 StartZ=0 EndX=41.65 EndY=-7.15 EndZ=0
    g4: LineSegment StartX=38.95 StartY=-7.15 StartZ=0 EndX=36.25 EndY=-7.15 EndZ=0
    g5: LineSegment StartX=36.25 StartY=-3.15 StartZ=0 EndX=36.25 EndY=-7.15 EndZ=0
  constraints (16):
    c: Horizontal(g0)
    c: Distance(g0) = 2.7
    c: Horizontal(g1)
    c: Distance(g1) = 2.7
    c: Coincident(g1,g0)
    c: Block(g0)
    c: Coincident(g2,g0)
    c: Vertical(g2)
    c: Horizontal(g3)
    c: Coincident(g3,g2)
    c: Horizontal(g4)
    c: Coincident(g5,g1)
    c: Vertical(g5)
    c: Coincident(g5,g4)
    c: Block(g3)
    c: Block(g4)
FEATURE [Sketcher::SketchObject] Sketch022
  FullyConstrained = true
  Placement = pos=(0,-14.3,2.37) rot=(-1,0,0;2.03453rad)
  sketch-geometry (6):
    g0: LineSegment StartX=41.65 StartY=-3.15 StartZ=0 EndX=38.95 EndY=-3.15 EndZ=0
    g1: LineSegment StartX=36.25 StartY=-3.15 StartZ=0 EndX=38.95 EndY=-3.15 EndZ=0
    g2: LineSegment StartX=41.65 StartY=-3.15 StartZ=0 EndX=41.65 EndY=-7.15 EndZ=0
    g3: LineSegment StartX=38.95 StartY=-7.15 StartZ=0 EndX=41.65 EndY=-7.15 EndZ=0
    g4: LineSegment StartX=38.95 StartY=-7.15 StartZ=0 EndX=36.25 EndY=-7.15 EndZ=0
    g5: LineSegment StartX=36.25 StartY=-3.15 StartZ=0 EndX=36.25 EndY=-7.15 EndZ=0
  constraints (16):
    c: Horizontal(g0)
    c: Distance(g0) = 2.7
    c: Horizontal(g1)
    c: Distance(g1) = 2.7
    c: Coincident(g1,g0)
    c: Block(g0)
    c: Coincident(g2,g0)
    c: Vertical(g2)
    c: Horizontal(g3)
    c: Coincident(g3,g2)
    c: Horizontal(g4)
    c: Coincident(g5,g1)
    c: Vertical(g5)
    c: Coincident(g5,g4)
    c: Block(g3)
    c: Block(g4)
FEATURE [Sketcher::SketchObject] Sketch024
  FullyConstrained = true
  Placement = pos=(0,-14.3,2.37) rot=(-1,0,0;2.03453rad)
  sketch-geometry (4):
    g0: LineSegment StartX=49.5 StartY=-21.2 StartZ=0 EndX=49.5 EndY=-22.8 EndZ=0
    g1: LineSegment StartX=49.5 StartY=-22.8 StartZ=0 EndX=0.002238 EndY=-22.8 EndZ=0
    g2: LineSegment StartX=0.002238 StartY=-21.2 StartZ=0 EndX=0.002238 EndY=-22.8 EndZ=0
    g3: LineSegment StartX=49.5 StartY=-21.2 StartZ=0 EndX=0.002238 EndY=-21.2 EndZ=0
  constraints (10):
    c: Vertical(g0)
    c: Distance(g0) = 1.6
    c: Coincident(g1,g0)
    c: Horizontal(g1)
    c: Vertical(g2)
    c: Coincident(g2,g1)
    c: Coincident(g3,g0)
    c: Coincident(g3,g2)
    c: Horizontal(g3)
    c: Block(g3)
FEATURE [Sketcher::SketchObject] Sketch025
  FullyConstrained = true
  Placement = pos=(0,-14.3,2.37) rot=(-1,0,0;2.03453rad)
  sketch-geometry (4):
    g0: LineSegment StartX=0 StartY=1.5 StartZ=0 EndX=0 EndY=0 EndZ=0
    g1: LineSegment StartX=0 StartY=1.5 StartZ=0 EndX=5 EndY=1.5 EndZ=0
    g2: LineSegment StartX=5 StartY=1.5 StartZ=0 EndX=5 EndY=0 EndZ=0
    g3: LineSegment StartX=0 StartY=0 StartZ=0 EndX=5 EndY=0 EndZ=0
  constraints (13):
    c: Vertical(g0)
    c: Distance(g0) = 1.5
    c: Horizontal(g1)
    c: Distance(g1) = 5
    c: Coincident(g1,g0)
    c: Vertical(g2)
    c: Distance(g2) = 1.5
    c: Coincident(g2,g1)
    c: Block(g1)
    c: Block(g2)
    c: Block(g0)
    c: Coincident(g3,g0)
    c: Coincident(g3,g2)
FEATURE [Part::Extrusion] Extrude022  label="solenoidDriverBottomLipTopExtrude014"
  Base = -> Sketch025
  Dir = (0,0.894389,-0.447291)
  DirMode = 2
  FaceMakerClass = Part::FaceMakerBullseye
  LengthFwd = -6.5
  LengthRev = 0
  Placement = pos=(0,-15.45,20.3) rot=(1,0,0;1.5708rad)
  Solid = true
  Symmetric = false
FEATURE [Part::Fillet] Fillet013  label="solenoidDriverBottomLipTopFillet006"
  Base = -> Extrude022
  Edges = 1 edges r=1.4: [Edge6]
  Placement = pos=(5,0,0) rot=(0,0,1;0rad)
FEATURE [Sketcher::SketchObject] Sketch026
  FullyConstrained = true
  Placement = pos=(0,-14.3,2.37) rot=(-1,0,0;2.03453rad)
  sketch-geometry (4):
    g0: LineSegment StartX=0 StartY=1.5 StartZ=0 EndX=0 EndY=0 EndZ=0
    g1: LineSegment StartX=0 StartY=1.5 StartZ=0 EndX=5 EndY=1.5 EndZ=0
    g2: LineSegment StartX=5 StartY=1.5 StartZ=0 EndX=5 EndY=0 EndZ=0
    g3: LineSegment StartX=0 StartY=0 StartZ=0 EndX=5 EndY=0 EndZ=0
  constraints (13):
    c: Vertical(g0)
    c: Distance(g0) = 1.5
    c: Horizontal(g1)
    c: Distance(g1) = 5
    c: Coincident(g1,g0)
    c: Vertical(g2)
    c: Distance(g2) = 1.5
    c: Coincident(g2,g1)
    c: Block(g1)
    c: Block(g2)
    c: Block(g0)
    c: Coincident(g3,g0)
    c: Coincident(g3,g2)
FEATURE [Part::Extrusion] Extrude023  label="solenoidDriverBottomLipTopExtrude015"
  Base = -> Sketch026
  Dir = (0,0.894389,-0.447291)
  DirMode = 2
  FaceMakerClass = Part::FaceMakerBullseye
  LengthFwd = -6.5
  LengthRev = 0
  Placement = pos=(5,-14.15,19.65) rot=(1,0,0;1.5708rad)
  Solid = true
  Symmetric = false
FEATURE [Sketcher::SketchObject] Sketch027
  FullyConstrained = true
  Placement = pos=(0,-14.3,2.37) rot=(-1,0,0;2.03453rad)
  sketch-geometry (5):
    g0: LineSegment StartX=45.5 StartY=-21.2 StartZ=0 EndX=49.5 EndY=-21.2 EndZ=0
    g1: LineSegment StartX=49.5 StartY=0 StartZ=0 EndX=49.5 EndY=-21.2 EndZ=0
    g2: LineSegment StartX=49.5 StartY=0 StartZ=0 EndX=49.5 EndY=1.6 EndZ=0
    g3: LineSegment StartX=45.5 StartY=-21.2 StartZ=0 EndX=45.5 EndY=1.6 EndZ=0
    g4: LineSegment StartX=49.5 StartY=1.6 StartZ=0 EndX=45.5 EndY=1.6 EndZ=0
  constraints (14):
    c: Horizontal(g0)
    c: Distance(g0) = 4
    c: Coincident(g1,g0)
    c: Vertical(g1)
    c: Block(g1)
    c: Vertical(g2)
    c: Distance(g2) = 1.6
    c: Block(g2)
    c: Coincident(g3,g0)
    c: Vertical(g3)
    c: Coincident(g4,g2)
    c: Horizontal(g4)
    c: Block(g0)
    c: Coincident(g3,g4)
FEATURE [Part::Extrusion] Extrude024
  Base = -> Sketch027
  Dir = (0,0.894389,-0.447291)
  DirMode = 2
  FaceMakerClass = Part::FaceMakerBullseye
  LengthFwd = 6.34
  LengthRev = 0
  Placement = pos=(0,-5.59,1) rot=(0,0,1;0rad)
  Solid = true
  Symmetric = false
FEATURE [Part::Fillet] Fillet014  label="solenoidDriverSideBarFillet014"
  Base = -> Extrude024
  Edges = 1 edges r=1.4: [Edge14]
  Placement = pos=(0,0.9,-0.45) rot=(0,0,1;0rad)
FEATURE [Part::Revolution] Revolve  label="mainScrewStandRevolve"
  Angle = 360
  Axis = (0,0,1)
  Base = (0,0,0)
  FaceMakerClass = Part::FaceMakerBullseye
  Placement = pos=(121.35,-15.3,0) rot=(0,0,1;0rad)
  Solid = true
  Source = -> Sketch004
  Symmetric = false
FEATURE [Part::Extrusion] Extrude021  label="solenoidDriverTopLipLowerExtrude011"
  Base = -> Sketch024
  Dir = (0,0.894389,-0.447291)
  DirMode = 2
  FaceMakerClass = Part::FaceMakerBullseye
  LengthFwd = 5.05
  LengthRev = 0
  Solid = true
  Symmetric = false
FEATURE [Part::Fillet] Fillet012  label="solenoidDriverTopLipLowerFillet004"
  Base = -> Extrude021
  Edges = 1 edges r=1.2: [Edge7]
  Placement = pos=(0,-0.9,-1.35) rot=(0,0,1;0rad)
FEATURE [Part::Fillet] Fillet003  label="solenoidDriverTopLipLowerFillet003"
  Base = -> Extrude010
  Edges = 1 edges r=1.2: [Edge7]
  Placement = pos=(0,-3,-0.3) rot=(0,0,1;0rad)
FEATURE [Part::Extrusion] Extrude025  label="mainBodyUpperExtrude025"
  Base = -> Sketch001
  Dir = (0,0,1)
  DirMode = 2
  FaceMakerClass = Part::FaceMakerBullseye
  LengthFwd = 20
  LengthRev = 0
  Solid = true
  Symmetric = false
FEATURE [Part::MultiFuse] Fusion  label="solenoidDriverBottomLipFusion"
  Placement = pos=(0,-1.6,0) rot=(0,0,1;0rad)
  Shapes = -> [Fillet005,Fillet013,Extrude023,Extrude013]
FEATURE [Sketcher::SketchObject] Sketch028
  FullyConstrained = true
  Placement = pos=(0,-14.3,2.37) rot=(-1,0,0;2.03453rad)
  sketch-geometry (4):
    g0: LineSegment StartX=0 StartY=1.5 StartZ=0 EndX=0 EndY=0 EndZ=0
    g1: LineSegment StartX=0 StartY=1.5 StartZ=0 EndX=5 EndY=1.5 EndZ=0
    g2: LineSegment StartX=5 StartY=1.5 StartZ=0 EndX=5 EndY=0 EndZ=0
    g3: LineSegment StartX=0 StartY=0 StartZ=0 EndX=5 EndY=0 EndZ=0
  constraints (13):
    c: Vertical(g0)
    c: Distance(g0) = 1.5
    c: Horizontal(g1)
    c: Distance(g1) = 5
    c: Coincident(g1,g0)
    c: Vertical(g2)
    c: Distance(g2) = 1.5
    c: Coincident(g2,g1)
    c: Block(g1)
    c: Block(g2)
    c: Block(g0)
    c: Coincident(g3,g0)
    c: Coincident(g3,g2)
FEATURE [Part::Extrusion] Extrude026  label="solenoidDriverBottomLipTopExtrude016"
  Base = -> Sketch028
  Dir = (0,0.894389,-0.447291)
  DirMode = 2
  FaceMakerClass = Part::FaceMakerBullseye
  LengthFwd = -6.5
  LengthRev = 0
  Placement = pos=(5,-14.15,19.65) rot=(1,0,0;1.5708rad)
  Solid = true
  Symmetric = false
FEATURE [Sketcher::SketchObject] Sketch029
  FullyConstrained = true
  Placement = pos=(0,-14.3,2.37) rot=(-1,0,0;2.03453rad)
  sketch-geometry (4):
    g0: LineSegment StartX=0 StartY=1.5 StartZ=0 EndX=0 EndY=0 EndZ=0
    g1: LineSegment StartX=0 StartY=1.5 StartZ=0 EndX=5 EndY=1.5 EndZ=0
    g2: LineSegment StartX=5 StartY=1.5 StartZ=0 EndX=5 EndY=0 EndZ=0
    g3: LineSegment StartX=0 StartY=0 StartZ=0 EndX=5 EndY=0 EndZ=0
  constraints (13):
    c: Vertical(g0)
    c: Distance(g0) = 1.5
    c: Horizontal(g1)
    c: Distance(g1) = 5
    c: Coincident(g1,g0)
    c: Vertical(g2)
    c: Distance(g2) = 1.5
    c: Coincident(g2,g1)
    c: Block(g1)
    c: Block(g2)
    c: Block(g0)
    c: Coincident(g3,g0)
    c: Coincident(g3,g2)
FEATURE [Part::Extrusion] Extrude027  label="solenoidDriverBottomLipTopExtrude017"
  Base = -> Sketch029
  Dir = (0,0.894389,-0.447291)
  DirMode = 2
  FaceMakerClass = Part::FaceMakerBullseye
  LengthFwd = -6.5
  LengthRev = 0
  Placement = pos=(0,-14.15,19.65) rot=(1,0,0;1.5708rad)
  Solid = true
  Symmetric = false
FEATURE [Sketcher::SketchObject] Sketch030
  FullyConstrained = true
  Placement = pos=(0,-14.3,2.37) rot=(-1,0,0;2.03453rad)
  sketch-geometry (4):
    g0: LineSegment StartX=0 StartY=1.5 StartZ=0 EndX=0 EndY=0 EndZ=0
    g1: LineSegment StartX=0 StartY=1.5 StartZ=0 EndX=5 EndY=1.5 EndZ=0
    g2: LineSegment StartX=5 StartY=1.5 StartZ=0 EndX=5 EndY=0 EndZ=0
    g3: LineSegment StartX=0 StartY=0 StartZ=0 EndX=5 EndY=0 EndZ=0
  constraints (13):
    c: Vertical(g0)
    c: Distance(g0) = 1.5
    c: Horizontal(g1)
    c: Distance(g1) = 5
    c: Coincident(g1,g0)
    c: Vertical(g2)
    c: Distance(g2) = 1.5
    c: Coincident(g2,g1)
    c: Block(g1)
    c: Block(g2)
    c: Block(g0)
    c: Coincident(g3,g0)
    c: Coincident(g3,g2)
FEATURE [Sketcher::SketchObject] Sketch031
  FullyConstrained = true
  Placement = pos=(0,-14.3,2.37) rot=(-1,0,0;2.03453rad)
  sketch-geometry (6):
    g0: LineSegment StartX=45.5 StartY=-21.2 StartZ=0 EndX=49.5 EndY=-21.2 EndZ=0
    g1: LineSegment StartX=45.5 StartY=0 StartZ=0 EndX=49.5 EndY=0 EndZ=0
    g2: LineSegment StartX=49.5 StartY=0 StartZ=0 EndX=49.5 EndY=-21.2 EndZ=0
    g3: LineSegment StartX=4 StartY=0 StartZ=0 EndX=4 EndY=-21.2 EndZ=0
    g4: LineSegment StartX=45.5 StartY=-21.2 StartZ=0 EndX=4 EndY=-21.2 EndZ=0
    g5: LineSegment StartX=4 StartY=0 StartZ=0 EndX=45.5 EndY=0 EndZ=0
  constraints (16):
    c: Horizontal(g0)
    c: Distance(g0) = 4
    c: Horizontal(g1)
    c: Distance(g1) = 4
    c: Coincident(g2,g1)
    c: Coincident(g2,g0)
    c: Vertical(g2)
    c: Block(g2)
    c: Vertical(g3)
    c: Coincident(g4,g0)
    c: Horizontal(g4)
    c: Coincident(g4,g3)
    c: Coincident(g5,g1)
    c: Horizontal(g5)
    c: Block(g3)
    c: Block(g5)
FEATURE [Part::Extrusion] Extrude028  label="removeFromSolenoidDriverMainExtrude021"
  Base = -> Sketch031
  Dir = (0,0.894389,-0.447291)
  DirMode = 2
  FaceMakerClass = Part::FaceMakerBullseye
  LengthFwd = 3.1
  LengthRev = 0
  Placement = pos=(-4,-2.42,-0.8) rot=(0,0,1;0rad)
  Solid = true
  Symmetric = false
FEATURE [Part::Extrusion] Extrude029  label="solenoidDriverBottomLipTopExtrude018"
  Base = -> Sketch030
  Dir = (0,0.894389,-0.447291)
  DirMode = 2
  FaceMakerClass = Part::FaceMakerBullseye
  LengthFwd = -6.5
  LengthRev = 0
  Placement = pos=(5,-14.15,19.65) rot=(1,0,0;1.5708rad)
  Solid = true
  Symmetric = false
FEATURE [Sketcher::SketchObject] Sketch032
  FullyConstrained = true
  Placement = pos=(0,-14.3,2.37) rot=(-1,0,0;2.03453rad)
  sketch-geometry (4):
    g0: LineSegment StartX=0 StartY=1.5 StartZ=0 EndX=0 EndY=0 EndZ=0
    g1: LineSegment StartX=0 StartY=1.5 StartZ=0 EndX=5 EndY=1.5 EndZ=0
    g2: LineSegment StartX=5 StartY=1.5 StartZ=0 EndX=5 EndY=0 EndZ=0
    g3: LineSegment StartX=0 StartY=0 StartZ=0 EndX=5 EndY=0 EndZ=0
  constraints (13):
    c: Vertical(g0)
    c: Distance(g0) = 1.5
    c: Horizontal(g1)
    c: Distance(g1) = 5
    c: Coincident(g1,g0)
    c: Vertical(g2)
    c: Distance(g2) = 1.5
    c: Coincident(g2,g1)
    c: Block(g1)
    c: Block(g2)
    c: Block(g0)
    c: Coincident(g3,g0)
    c: Coincident(g3,g2)
FEATURE [Part::Extrusion] Extrude030  label="solenoidDriverBottomLipTopExtrude019"
  Base = -> Sketch032
  Dir = (0,0.894389,-0.447291)
  DirMode = 2
  FaceMakerClass = Part::FaceMakerBullseye
  LengthFwd = -6.5
  LengthRev = 0
  Placement = pos=(0,-14.15,19.65) rot=(1,0,0;1.5708rad)
  Solid = true
  Symmetric = false
FEATURE [Part::MultiFuse] Fusion004
  Placement = pos=(0,1.4,2.65) rot=(0,0,1;0rad)
  Shapes = -> [Extrude029,Extrude030]
FEATURE [Part::MultiFuse] Fusion003
  Placement = pos=(-2.3,0,0) rot=(0,0,1;0rad)
  Shapes = -> [Extrude028,Fusion004]
FEATURE [Sketcher::SketchObject] Sketch033
  FullyConstrained = true
  Placement = pos=(0,-14.3,2.37) rot=(-1,0,0;2.03453rad)
  sketch-geometry (4):
    g0: LineSegment StartX=0 StartY=1.5 StartZ=0 EndX=0 EndY=0 EndZ=0
    g1: LineSegment StartX=0 StartY=1.5 StartZ=0 EndX=5 EndY=1.5 EndZ=0
    g2: LineSegment StartX=5 StartY=1.5 StartZ=0 EndX=5 EndY=0 EndZ=0
    g3: LineSegment StartX=0 StartY=0 StartZ=0 EndX=5 EndY=0 EndZ=0
  constraints (13):
    c: Vertical(g0)
    c: Distance(g0) = 1.5
    c: Horizontal(g1)
    c: Distance(g1) = 5
    c: Coincident(g1,g0)
    c: Vertical(g2)
    c: Distance(g2) = 1.5
    c: Coincident(g2,g1)
    c: Block(g1)
    c: Block(g2)
    c: Block(g0)
    c: Coincident(g3,g0)
    c: Coincident(g3,g2)
FEATURE [Sketcher::SketchObject] Sketch034
  FullyConstrained = true
  Placement = pos=(0,-14.3,2.37) rot=(-1,0,0;2.03453rad)
  sketch-geometry (4):
    g0: LineSegment StartX=0 StartY=1.5 StartZ=0 EndX=4 EndY=1.5 EndZ=0
    g1: LineSegment StartX=4 StartY=1.5 StartZ=0 EndX=4 EndY=-2.5 EndZ=0
    g2: LineSegment StartX=4 StartY=-2.5 StartZ=0 EndX=0 EndY=-2.5 EndZ=0
    g3: LineSegment StartX=0 StartY=1.5 StartZ=0 EndX=0 EndY=-2.5 EndZ=0
  constraints (11):
    c: Horizontal(g0)
    c: Distance(g0) = 4
    c: Block(g0)
    c: Coincident(g1,g0)
    c: Vertical(g1)
    c: Distance(g1) = 4
    c: Coincident(g2,g1)
    c: Horizontal(g2)
    c: Distance(g2) = 4
    c: Coincident(g3,g0)
    c: Coincident(g3,g2)
FEATURE [Part::Extrusion] Extrude020  label="removeFromSolenoidDriverMainExtrude020"
  Base = -> Sketch020
  Dir = (0,0.894389,-0.447291)
  DirMode = 2
  FaceMakerClass = Part::FaceMakerBullseye
  LengthFwd = 3.1
  LengthRev = 0
  Placement = pos=(-4,-2.42,-0.8) rot=(0,0,1;0rad)
  Solid = true
  Symmetric = false
FEATURE [Part::Fillet] Fillet
  Base = -> Fusion003
  Edges = 1 edges r=10: [Edge5]
  Placement = pos=(-2,0,0) rot=(0,0,1;0rad)
FEATURE [Part::MultiFuse] Fusion001
  Placement = pos=(0,1.4,2.65) rot=(0,0,1;0rad)
  Shapes = -> [Extrude026,Extrude027]
FEATURE [Part::MultiFuse] Fusion002
  Shapes = -> [Extrude020,Fusion001]
FEATURE [Sketcher::SketchObject] Sketch035
  FullyConstrained = true
  Placement = pos=(0,-14.3,2.37) rot=(-1,0,0;2.03453rad)
  sketch-geometry (4):
    g0: LineSegment StartX=0 StartY=1.5 StartZ=0 EndX=0 EndY=0 EndZ=0
    g1: LineSegment StartX=0 StartY=1.5 StartZ=0 EndX=5 EndY=1.5 EndZ=0
    g2: LineSegment StartX=5 StartY=1.5 StartZ=0 EndX=5 EndY=0 EndZ=0
    g3: LineSegment StartX=0 StartY=0 StartZ=0 EndX=5 EndY=0 EndZ=0
  constraints (13):
    c: Vertical(g0)
    c: Distance(g0) = 1.5
    c: Horizontal(g1)
    c: Distance(g1) = 5
    c: Coincident(g1,g0)
    c: Vertical(g2)
    c: Distance(g2) = 1.5
    c: Coincident(g2,g1)
    c: Block(g1)
    c: Block(g2)
    c: Block(g0)
    c: Coincident(g3,g0)
    c: Coincident(g3,g2)
FEATURE [Sketcher::SketchObject] Sketch036
  FullyConstrained = true
  Placement = pos=(0,-14.3,2.37) rot=(-1,0,0;2.03453rad)
  sketch-geometry (4):
    g0: LineSegment StartX=0 StartY=1.5 StartZ=0 EndX=0 EndY=0 EndZ=0
    g1: LineSegment StartX=0 StartY=1.5 StartZ=0 EndX=5 EndY=1.5 EndZ=0
    g2: LineSegment StartX=5 StartY=1.5 StartZ=0 EndX=5 EndY=0 EndZ=0
    g3: LineSegment StartX=0 StartY=0 StartZ=0 EndX=5 EndY=0 EndZ=0
  constraints (13):
    c: Vertical(g0)
    c: Distance(g0) = 1.5
    c: Horizontal(g1)
    c: Distance(g1) = 5
    c: Coincident(g1,g0)
    c: Vertical(g2)
    c: Distance(g2) = 1.5
    c: Coincident(g2,g1)
    c: Block(g1)
    c: Block(g2)
    c: Block(g0)
    c: Coincident(g3,g0)
    c: Coincident(g3,g2)
FEATURE [Part::Extrusion] Extrude031  label="solenoidDriverBottomLipTopExtrude020"
  Base = -> Sketch035
  Dir = (0,0.894389,-0.447291)
  DirMode = 2
  FaceMakerClass = Part::FaceMakerBullseye
  LengthFwd = -6.5
  LengthRev = 0
  Placement = pos=(5,-14.15,19.65) rot=(1,0,0;1.5708rad)
  Solid = true
  Symmetric = false
FEATURE [Part::Extrusion] Extrude032  label="solenoidDriverBottomLipTopExtrude021"
  Base = -> Sketch036
  Dir = (0,0.894389,-0.447291)
  DirMode = 2
  FaceMakerClass = Part::FaceMakerBullseye
  LengthFwd = -6.5
  LengthRev = 0
  Placement = pos=(0,-14.15,19.65) rot=(1,0,0;1.5708rad)
  Solid = true
  Symmetric = false
FEATURE [Part::MultiFuse] Fusion009
  Placement = pos=(8,1.4,2.65) rot=(0,0,1;0rad)
  Shapes = -> [Extrude031,Extrude032]
FEATURE [Part::MultiFuse] Fusion010  label="removeFromSolenoidDriver"
  Shapes = -> [Fusion009,Fillet,Fusion002]
FEATURE [Sketcher::SketchObject] Sketch037
  FullyConstrained = true
  Placement = pos=(0,0,0) rot=(1,0,0;1.5708rad)
  sketch-geometry (4):
    g0: Circle CenterX=64.05 CenterY=16.5 CenterZ=0 NormalX=0 NormalY=0 NormalZ=1 AngleXU=0 Radius=2.7
    g1: Circle CenterX=64.05 CenterY=8.5 CenterZ=0 NormalX=0 NormalY=0 NormalZ=1 AngleXU=0 Radius=2.7
    g2: Circle CenterX=84.15 CenterY=8.5 CenterZ=0 NormalX=0 NormalY=0 NormalZ=1 AngleXU=0 Radius=2.7
    g3: Circle CenterX=84.15 CenterY=16.5 CenterZ=0 NormalX=0 NormalY=0 NormalZ=1 AngleXU=0 Radius=2.7
  constraints (4):
    c: Block(g2)
    c: Block(g3)
    c: Block(g0)
    c: Block(g1)
FEATURE [Part::Extrusion] Extrude033  label="removeFromMainBodyToCreateScrewHoleCounterSinks001"
  Base = -> Sketch037
  Dir = (0,-1,1.1e-15)
  DirMode = 2
  FaceMakerClass = Part::FaceMakerBullseye
  LengthFwd = 1.9
  LengthRev = 0
  Placement = pos=(0.8,0,0) rot=(0,0,1;0rad)
  Solid = true
  Symmetric = false
FEATURE [Part::MultiFuse] Fusion011  label="removeFromMainBodyToCreateScrewHoleCounterSinks001Fusion011"
  Shapes = -> [Extrude014,Extrude033]
FEATURE [Sketcher::SketchObject] Sketch038
  FullyConstrained = true
  Placement = pos=(0,-14.3,2.37) rot=(-1,0,0;2.03453rad)
  sketch-geometry (4):
    g0: LineSegment StartX=33.9 StartY=-9.7 StartZ=0 EndX=33.9 EndY=-1.5 EndZ=0
    g1: LineSegment StartX=33.9 StartY=-1.5 StartZ=0 EndX=44.5 EndY=-1.5 EndZ=0
    g2: LineSegment StartX=33.9 StartY=-9.7 StartZ=0 EndX=44.5 EndY=-9.7 EndZ=0
    g3: LineSegment StartX=44.5 StartY=-1.5 StartZ=0 EndX=44.5 EndY=-9.7 EndZ=0
  constraints (10):
    c: Vertical(g0)
    c: Coincident(g1,g0)
    c: Horizontal(g1)
    c: Block(g1)
    c: Block(g0)
    c: Coincident(g2,g0)
    c: Horizontal(g2)
    c: Coincident(g3,g1)
    c: Coincident(g3,g2)
    c: Vertical(g3)
FEATURE [Part::Extrusion] Extrude034
  Base = -> Sketch038
  Dir = (0,0.894389,-0.447291)
  DirMode = 2
  FaceMakerClass = Part::FaceMakerBullseye
  LengthFwd = 16
  LengthRev = 0
  Placement = pos=(0,-22,7) rot=(0,0,1;0rad)
  Solid = true
  Symmetric = false
FEATURE [Sketcher::SketchObject] Sketch039
  FullyConstrained = true
  Placement = pos=(0,-14.3,2.37) rot=(-1,0,0;2.03453rad)
  sketch-geometry (4):
    g0: LineSegment StartX=5.5 StartY=-7.7 StartZ=0 EndX=13.3 EndY=-7.7 EndZ=0
    g1: LineSegment StartX=13.3 StartY=-7.7 StartZ=0 EndX=13.3 EndY=-13.1 EndZ=0
    g2: LineSegment StartX=13.3 StartY=-13.1 StartZ=0 EndX=5.5 EndY=-13.1 EndZ=0
    g3: LineSegment StartX=5.5 StartY=-7.7 StartZ=0 EndX=5.5 EndY=-13.1 EndZ=0
  constraints (12):
    c: Horizontal(g0)
    c: Distance(g0) = 7.8
    c: Coincident(g1,g0)
    c: Vertical(g1)
    c: Distance(g1) = 5.4
    c: Coincident(g2,g1)
    c: Horizontal(g2)
    c: Vertical(g3)
    c: Coincident(g3,g2)
    c: Block(g0)
    c: Block(g2)
    c: Block(g3)
FEATURE [Part::Extrusion] Extrude035  label="removeToMakeHoleForConnectorExtrude035"
  Base = -> Sketch039
  Dir = (0,0.894389,-0.447291)
  DirMode = 2
  FaceMakerClass = Part::FaceMakerBullseye
  LengthFwd = 15
  LengthRev = 0
  Placement = pos=(-4,-22,9.6469) rot=(0,0,1;0rad)
  Solid = true
  Symmetric = false
FEATURE [App::MeasureDistance] Distance  label="Distance: 4.00 mm"
  Distance = 4.00184
  P1 = (119.349,-15.3,8)
  P2 = (123.351,-15.3,8)
FEATURE [App::MeasureDistance] Distance001  label="Distance: 3.80 mm"
  Distance = 3.8
  P1 = (119.45,-15.3,8)
  P2 = (123.25,-15.3,8)
FEATURE [Part::Fillet] Fillet015
  Base = -> Extrude009
  Edges = 1 edges r=1.59: [Edge7]
FEATURE [Part::Fillet] Fillet016
  Base = -> Extrude017
  Edges = 1 edges r=1.49: [Edge12]
FEATURE [Part::Fillet] Fillet017
  Base = -> Fillet016
  Edges = 1 edges r=1.45: [Edge8]
FEATURE [Part::MultiFuse] Fusion012  label="main"
  Shapes = -> [Extrude,Revolve,Extrude005,Fillet003,Fillet012,Fillet014,Extrude025,Fusion,Fillet015,Fillet017]
FEATURE [Part::Cut] Cut001
  Base = -> Fusion012
  Tool = -> Box003
FEATURE [Part::Cut] Cut002
  Base = -> Cut001
  Tool = -> Box002
FEATURE [Part::Cut] Cut003
  Base = -> Cut002
  Tool = -> Cut
FEATURE [Part::Cut] Cut004
  Base = -> Cut003
  Tool = -> Extrude019
FEATURE [Part::Cut] Cut005
  Base = -> Cut004
  Tool = -> Fusion011
FEATURE [Part::Cut] Cut006
  Base = -> Cut005
  Tool = -> Extrude004
FEATURE [Part::Cut] Cut007
  Base = -> Cut006
  Tool = -> Extrude015
FEATURE [Part::Cut] Cut008
  Base = -> Cut007
  Tool = -> Extrude008
FEATURE [Part::Cut] Cut009
  Base = -> Cut008
  Tool = -> Fusion010
FEATURE [App::MeasureDistance] Distance002  label="Distance: 2.05 mm"
  Distance = 2.05453
  P1 = (1.5,-23.0732,21.402)
  P2 = (6e-15,-23,20)
FEATURE [Part::Cut] Cut010
  Base = -> Cut009
  Tool = -> Extrude035
FEATURE [Part::Cut] Cut011
  Base = -> Cut010
  Tool = -> Extrude034
FEATURE [Part::Box] Box004  label="Cube004"
  AttacherType = Attacher::AttachEngine3D
  Height = 10
  Length = 200
  Placement = pos=(-30,0,0) rot=(0,0,1;0rad)
  Width = 10
FEATURE [Part::Fillet] Fillet020
  Base = -> Box004
  Edges = 1 edges r=3.6: [Edge12]
FEATURE [Part::Box] Box005  label="Cube005"
  AttacherType = Attacher::AttachEngine3D
  Height = 10
  Length = 198
  Placement = pos=(-30,0,0) rot=(0,0,1;0rad)
  Width = 10
FEATURE [Part::Cut] Cut012
  Base = -> Box005
  Tool = -> Fillet020
FEATURE [Part::Box] Box006  label="Cube006"
  AttacherType = Attacher::AttachEngine3D
  Height = 5
  Length = 200
  Placement = pos=(-30,6.4,10) rot=(1,0,0;0rad)
  Width = 5
FEATURE [Part::Box] Box007  label="Cube007"
  AttacherType = Attacher::AttachEngine3D
  Height = 5
  Length = 200
  Placement = pos=(-30,6.4,10) rot=(1,0,0;0.872665rad)
  Width = 5
FEATURE [Part::MultiFuse] Fusion013  label="removeFromMainFusion013"
  Placement = pos=(0,-10,10) rot=(0,0,1;0rad)
  Shapes = -> [Box007,Box006,Cut012]
FEATURE [Mesh::Feature] v0_98_Cut013  label="v0_98-Cut013"
FEATURE [App::MeasureDistance] Distance003  label="Distance: 7.18 mm"
  Distance = 7.17719
  P1 = (117.773,-15.3145,-2.4)
  P2 = (124.951,-15.2973,-2.4)
FEATURE [Sketcher::SketchObject] Sketch040
  FullyConstrained = true
  Placement = pos=(0,-14.3,2.37) rot=(-1,0,0;2.03453rad)
  sketch-geometry (4):
    g0: LineSegment StartX=0 StartY=1.5 StartZ=0 EndX=0 EndY=0 EndZ=0
    g1: LineSegment StartX=0 StartY=1.5 StartZ=0 EndX=5 EndY=1.5 EndZ=0
    g2: LineSegment StartX=5 StartY=1.5 StartZ=0 EndX=5 EndY=0 EndZ=0
    g3: LineSegment StartX=0 StartY=0 StartZ=0 EndX=5 EndY=0 EndZ=0
  constraints (13):
    c: Vertical(g0)
    c: Distance(g0) = 1.5
    c: Horizontal(g1)
    c: Distance(g1) = 5
    c: Coincident(g1,g0)
    c: Vertical(g2)
    c: Distance(g2) = 1.5
    c: Coincident(g2,g1)
    c: Block(g1)
    c: Block(g2)
    c: Block(g0)
    c: Coincident(g3,g0)
    c: Coincident(g3,g2)
FEATURE [Part::Extrusion] Extrude036
  Base = -> Sketch040
  Dir = (0,0.894389,-0.447291)
  DirMode = 2
  FaceMakerClass = Part::FaceMakerBullseye
  LengthFwd = 1.4
  LengthRev = 0
  Placement = pos=(0,8.25,17.58) rot=(0,0,1;0rad)
  Solid = true
  Symmetric = false
FEATURE [Sketcher::SketchObject] Sketch041
  FullyConstrained = true
  Placement = pos=(0,-14.3,2.37) rot=(-1,0,0;2.03453rad)
  sketch-geometry (4):
    g0: LineSegment StartX=0 StartY=1.5 StartZ=0 EndX=0 EndY=0 EndZ=0
    g1: LineSegment StartX=0 StartY=1.5 StartZ=0 EndX=5 EndY=1.5 EndZ=0
    g2: LineSegment StartX=5 StartY=1.5 StartZ=0 EndX=5 EndY=0 EndZ=0
    g3: LineSegment StartX=0 StartY=0 StartZ=0 EndX=5 EndY=0 EndZ=0
  constraints (13):
    c: Vertical(g0)
    c: Distance(g0) = 1.5
    c: Horizontal(g1)
    c: Distance(g1) = 5
    c: Coincident(g1,g0)
    c: Vertical(g2)
    c: Distance(g2) = 1.5
    c: Coincident(g2,g1)
    c: Block(g1)
    c: Block(g2)
    c: Block(g0)
    c: Coincident(g3,g0)
    c: Coincident(g3,g2)
FEATURE [Part::Extrusion] Extrude037
  Base = -> Sketch041
  Dir = (0,0.894389,-0.447291)
  DirMode = 2
  FaceMakerClass = Part::FaceMakerBullseye
  LengthFwd = 1.4
  LengthRev = 0
  Placement = pos=(0,6.11,13.33) rot=(0,0,1;0rad)
  Solid = true
  Symmetric = false
FEATURE [Part::MultiFuse] Fusion014  label="screwSpacerFusion014"
  Shapes = -> [Extrude037,Extrude036]
FEATURE [Sketcher::SketchObject] Sketch042
  FullyConstrained = true
  Placement = pos=(0,-14.3,2.37) rot=(-1,0,0;2.03453rad)
  sketch-geometry (4):
    g0: LineSegment StartX=0 StartY=1.5 StartZ=0 EndX=0 EndY=0 EndZ=0
    g1: LineSegment StartX=0 StartY=1.5 StartZ=0 EndX=5 EndY=1.5 EndZ=0
    g2: LineSegment StartX=5 StartY=1.5 StartZ=0 EndX=5 EndY=0 EndZ=0
    g3: LineSegment StartX=0 StartY=0 StartZ=0 EndX=5 EndY=0 EndZ=0
  constraints (13):
    c: Vertical(g0)
    c: Distance(g0) = 1.5
    c: Horizontal(g1)
    c: Distance(g1) = 5
    c: Coincident(g1,g0)
    c: Vertical(g2)
    c: Distance(g2) = 1.5
    c: Coincident(g2,g1)
    c: Block(g1)
    c: Block(g2)
    c: Block(g0)
    c: Coincident(g3,g0)
    c: Coincident(g3,g2)
FEATURE [Part::Extrusion] Extrude038
  Base = -> Sketch042
  Dir = (0,0.894389,-0.447291)
  DirMode = 2
  FaceMakerClass = Part::FaceMakerBullseye
  LengthFwd = 1.4
  LengthRev = 0
  Placement = pos=(0,8.459,18) rot=(0,0,1;0rad)
  Solid = true
  Symmetric = false
FEATURE [Part::MultiFuse] Fusion015  label="screwSpacerFusion014Fusion015"
  Placement = pos=(0,0.35,-0.18) rot=(0,0,1;0rad)
  Shapes = -> [Extrude038,Fusion014]
FEATURE [Part::Cylinder] Cylinder
  Angle = 360
  AttacherType = Attacher::AttachEngine3D
  Height = 10
  Placement = pos=(0,10,0) rot=(0,0,1;0rad)
  Radius = 1.5
FEATURE [Part::Cylinder] Cylinder001
  Angle = 360
  AttacherType = Attacher::AttachEngine3D
  Height = 10
  Placement = pos=(3,10,0) rot=(0,0,1;0rad)
  Radius = 1.5
FEATURE [Part::Box] Box008  label="Cube008"
  AttacherType = Attacher::AttachEngine3D
  Height = 10
  Length = 3
  Placement = pos=(0,8.5,0) rot=(0,0,1;0rad)
  Width = 3
FEATURE [Part::MultiFuse] Fusion016  label="holeForWireFusion016"
  Shapes = -> [Cylinder001,Box008,Cylinder]
FEATURE [Part::Box] Box009  label="Cube009"
  AttacherType = Attacher::AttachEngine3D
  Height = 10
  Length = 3
  Placement = pos=(0,8.5,0) rot=(0,0,1;0rad)
  Width = 3
FEATURE [Part::Cylinder] Cylinder002
  Angle = 360
  AttacherType = Attacher::AttachEngine3D
  Height = 10
  Placement = pos=(0,10,0) rot=(0,0,1;0rad)
  Radius = 1.5
FEATURE [Part::Cylinder] Cylinder003
  Angle = 360
  AttacherType = Attacher::AttachEngine3D
  Height = 10
  Placement = pos=(3,10,0) rot=(0,0,1;0rad)
  Radius = 1.5
FEATURE [Part::MultiFuse] Fusion017  label="holeForWireFusion017"
  Placement = pos=(0,0,10) rot=(0,0,1;0rad)
  Shapes = -> [Cylinder003,Box009,Cylinder002]
FEATURE [Part::MultiFuse] Fusion018  label="holeForWireFusion018"
  Placement = pos=(0,0,0) rot=(0,1,0;-1.5708rad)
  Shapes = -> [Fusion017,Fusion016]
FEATURE [Part::Box] Box010  label="Cube010"
  AttacherType = Attacher::AttachEngine3D
  Height = 0.1
  Length = 0.1
  Placement = pos=(-2,10,0) rot=(0,0.995037,0.099504;0rad)
  Width = 0.1
FEATURE [Part::MultiFuse] Fusion019
  Placement = pos=(0,10,0) rot=(1,0,0;1.5708rad)
  Shapes = -> [Box010,Fusion018]
FEATURE [Part::Box] Box011  label="Cube011"
  AttacherType = Attacher::AttachEngine3D
  Height = 0.1
  Length = 1.1
  Placement = pos=(-2,10,10) rot=(0,0.995037,0.099504;0rad)
  Width = 0.1
FEATURE [Part::MultiFuse] Fusion020
  Placement = pos=(0,0,0) rot=(0,1,0;0.349066rad)
  Shapes = -> [Box011,Fusion019]
FEATURE [Part::Box] Box012  label="Cube012"
  AttacherType = Attacher::AttachEngine3D
  Height = 0.1
  Length = 1.1
  Placement = pos=(-2,10,10) rot=(0,0.995037,0.099504;0rad)
  Width = 0.1
FEATURE [Part::MultiFuse] Fusion021
  Placement = pos=(0,30,0) rot=(0,0,1;-2.6529rad)
  Shapes = -> [Box012,Fusion020]
FEATURE [Part::Box] Box013  label="Cube013"
  AttacherType = Attacher::AttachEngine3D
  Height = 0.1
  Length = 1.1
  Placement = pos=(2,19,10) rot=(0,0.995037,0.099504;0rad)
  Width = 0.1
FEATURE [Part::MultiFuse] Fusion022  label="holeForWire"
  Placement = pos=(15,-49.8,-8.2) rot=(0,0,1;0rad)
  Shapes = -> [Box013,Fusion021]
FEATURE [Part::Cut] Cut013
  Base = -> Cut011
  Tool = -> Fusion013
FEATURE [Part::Cut] Cut014
  Base = -> Cut013
  Tool = -> Fusion022
FEATURE [Sketcher::SketchObject] Sketch043
  FullyConstrained = true
  MapMode = 4
  Placement = pos=(0,0,0) rot=(0.57735,0.57735,0.57735;2.0944rad)
  Support = -> [Cut014]
  sketch-geometry (14):
    g0: LineSegment StartX=6.08745 StartY=-4.11588 StartZ=0 EndX=6.08745 EndY=-2.11589 EndZ=0
    g1: LineSegment StartX=3.58745 StartY=2.38411 StartZ=0 EndX=3.58745 EndY=4.38411 EndZ=0
    g2: LineSegment StartX=8.08745 StartY=1.38411 StartZ=0 EndX=8.08745 EndY=-1.11589 EndZ=0
    g3: ArcOfCircle CenterX=7.08745 CenterY=-1.11589 CenterZ=0 NormalX=0 NormalY=0 NormalZ=1 AngleXU=0 Radius=1 StartAngle=4.71239 EndAngle=6.28319
    g4: LineSegment StartX=6.08745 StartY=-2.11589 StartZ=0 EndX=7.08745 EndY=-2.11589 EndZ=0
    g5: LineSegment StartX=6.08745 StartY=-4.11588 StartZ=0 EndX=7.08745 EndY=-4.11588 EndZ=0
    g6: ArcOfCircle CenterX=7.08745 CenterY=-1.11589 CenterZ=0 NormalX=0 NormalY=0 NormalZ=1 AngleXU=0 Radius=3 StartAngle=4.71239 EndAngle=6.28319
    g7: ArcOfCircle CenterX=7.08745 CenterY=1.38411 CenterZ=0 NormalX=0 NormalY=0 NormalZ=1 AngleXU=0 Radius=1 StartAngle=5.35e-14 EndAngle=1.5708
    g8: LineSegment StartX=3.58745 StartY=4.38411 StartZ=0 EndX=7.08745 EndY=4.38411 EndZ=0
    g9: LineSegment StartX=10.0875 StartY=-1.11588 StartZ=0 EndX=10.0875 EndY=1.38411 EndZ=0
    g10: ArcOfCircle CenterX=7.08745 CenterY=1.38411 CenterZ=0 NormalX=0 NormalY=0 NormalZ=1 AngleXU=0 Radius=3 StartAngle=3.57e-14 EndAngle=1.5708
    g11: LineSegment StartX=3.58745 StartY=2.38411 StartZ=0 EndX=3.58745 EndY=1.38411 EndZ=0
    g12: ArcOfCircle CenterX=4.58745 CenterY=1.38412 CenterZ=0 NormalX=0 NormalY=0 NormalZ=1 AngleXU=0 Radius=1 StartAngle=1.57081 EndAngle=3.14159
    g13: LineSegment StartX=4.58744 StartY=2.38411 StartZ=0 EndX=7.08745 EndY=2.38411 EndZ=0
  constraints (33):
    c: Vertical(g0)
    c: Vertical(g1)
    c: Distance(g1) = 2
    c: Block(g0)
    c: Block(g2)
    c: Coincident(g3,g2)
    c: Coincident(g4,g0)
    c: Coincident(g4,g3)
    c: Horizontal(g4)
    c: Block(g3)
    c: Coincident(g5,g0)
    c: Horizontal(g5)
    c: Coincident(g6,g3)
    c: Block(g6)
    c: Block(g5)
    c: Coincident(g7,g2)
    c: Block(g7)
    c: Coincident(g8,g1)
    c: Coincident(g9,g6)
    c: Vertical(g9)
    c: Coincident(g10,g7)
    c: Block(g10)
    c: Block(g8)
    c: Block(g9)
    c: Coincident(g11,g1)
    c: Vertical(g11)
    c: Distance(g11) = 1
    c: Coincident(g12,g11)
    c: Coincident(g13,g12)
    c: Coincident(g13,g7)
    c: Horizontal(g13)
    c: Block(g13)
    c: Block(g12)
FEATURE [Sketcher::SketchObject] Sketch044
  FullyConstrained = true
  MapMode = 4
  Placement = pos=(0,0,0) rot=(0.57735,0.57735,0.57735;2.0944rad)
  Support = -> [Cut014]
  sketch-geometry (14):
    g0: LineSegment StartX=6.08745 StartY=-4.11588 StartZ=0 EndX=6.08745 EndY=-2.11589 EndZ=0
    g1: LineSegment StartX=8.08745 StartY=1.38411 StartZ=0 EndX=8.08745 EndY=-1.11589 EndZ=0
    g2: ArcOfCircle CenterX=7.08745 CenterY=-1.11589 CenterZ=0 NormalX=0 NormalY=0 NormalZ=1 AngleXU=0 Radius=1 StartAngle=4.71239 EndAngle=6.28319
    g3: LineSegment StartX=6.08745 StartY=-2.11589 StartZ=0 EndX=7.08745 EndY=-2.11589 EndZ=0
    g4: LineSegment StartX=6.08745 StartY=-4.11588 StartZ=0 EndX=7.08745 EndY=-4.11588 EndZ=0
    g5: ArcOfCircle CenterX=7.08745 CenterY=-1.11589 CenterZ=0 NormalX=0 NormalY=0 NormalZ=1 AngleXU=0 Radius=3 StartAngle=4.71239 EndAngle=6.28319
    g6: ArcOfCircle CenterX=7.08745 CenterY=1.38411 CenterZ=0 NormalX=0 NormalY=0 NormalZ=1 AngleXU=0 Radius=1 StartAngle=5.35e-14 EndAngle=1.5708
    g7: LineSegment StartX=10.0875 StartY=-1.11588 StartZ=0 EndX=10.0875 EndY=1.38411 EndZ=0
    g8: ArcOfCircle CenterX=7.08745 CenterY=1.38411 CenterZ=0 NormalX=0 NormalY=0 NormalZ=1 AngleXU=0 Radius=3 StartAngle=3.57e-14 EndAngle=1.5708
    g9: ArcOfCircle CenterX=4.58745 CenterY=1.38412 CenterZ=0 NormalX=0 NormalY=0 NormalZ=1 AngleXU=0 Radius=1 StartAngle=1.57081 EndAngle=3.14159
    g10: LineSegment StartX=4.58744 StartY=2.38411 StartZ=0 EndX=7.08745 EndY=2.38411 EndZ=0
    g11: LineSegment StartX=4.58745 StartY=4.38411 StartZ=0 EndX=7.08745 EndY=4.38411 EndZ=0
    g12: ArcOfCircle CenterX=4.58745 CenterY=5.38411 CenterZ=0 NormalX=0 NormalY=0 NormalZ=1 AngleXU=0 Radius=1 StartAngle=3.14159 EndAngle=4.71239
    g13: LineSegment StartX=3.58745 StartY=5.38411 StartZ=0 EndX=3.58745 EndY=1.38411 EndZ=0
  constraints (33):
    c: Vertical(g0)
    c: Block(g0)
    c: Block(g1)
    c: Coincident(g2,g1)
    c: Coincident(g3,g0)
    c: Coincident(g3,g2)
    c: Horizontal(g3)
    c: Block(g2)
    c: Coincident(g4,g0)
    c: Horizontal(g4)
    c: Coincident(g5,g2)
    c: Block(g5)
    c: Block(g4)
    c: Coincident(g6,g1)
    c: Block(g6)
    c: Coincident(g7,g5)
    c: Vertical(g7)
    c: Coincident(g8,g6)
    c: Block(g8)
    c: Block(g7)
    c: Coincident(g10,g9)
    c: Coincident(g10,g6)
    c: Horizontal(g10)
    c: Block(g10)
    c: Block(g9)
    c: Coincident(g11,g8)
    c: Horizontal(g11)
    c: Block(g12)
    c: Block(g11)
    c: Coincident(g13,g12)
    c: Coincident(g13,g9)
    c: Vertical(g13)
    c: Tangent(g13,g9)
FEATURE [Part::Extrusion] Extrude039
  Base = -> Sketch044
  Dir = (1,0,0)
  DirMode = 2
  FaceMakerClass = Part::FaceMakerBullseye
  LengthFwd = 10
  LengthRev = 0
  Placement = pos=(8,-22.615,4.115) rot=(0,0,1;3.14159rad)
  Solid = true
  Symmetric = false
FEATURE [App::MeasureDistance] Distance004  label="Distance: 42.16 mm"
  Distance = 42.1607
  P1 = (14.6786,-26.2,1.24491)
  P2 = (-27.4815,-26.2,1.03853)
FEATURE [Sketcher::SketchObject] Sketch045
  FullyConstrained = true
  MapMode = 4
  Placement = pos=(0,0,0) rot=(0.57735,0.57735,0.57735;2.0944rad)
  Support = -> [Cut014]
  sketch-geometry (14):
    g0: LineSegment StartX=6.08745 StartY=-4.11588 StartZ=0 EndX=6.08745 EndY=-2.11589 EndZ=0
    g1: LineSegment StartX=8.08745 StartY=1.38411 StartZ=0 EndX=8.08745 EndY=-1.11589 EndZ=0
    g2: ArcOfCircle CenterX=7.08745 CenterY=-1.11589 CenterZ=0 NormalX=0 NormalY=0 NormalZ=1 AngleXU=0 Radius=1 StartAngle=4.71239 EndAngle=6.28319
    g3: LineSegment StartX=6.08745 StartY=-2.11589 StartZ=0 EndX=7.08745 EndY=-2.11589 EndZ=0
    g4: LineSegment StartX=6.08745 StartY=-4.11588 StartZ=0 EndX=7.08745 EndY=-4.11588 EndZ=0
    g5: ArcOfCircle CenterX=7.08745 CenterY=-1.11589 CenterZ=0 NormalX=0 NormalY=0 NormalZ=1 AngleXU=0 Radius=3 StartAngle=4.71239 EndAngle=6.28319
    g6: ArcOfCircle CenterX=7.08745 CenterY=1.38411 CenterZ=0 NormalX=0 NormalY=0 NormalZ=1 AngleXU=0 Radius=1 StartAngle=5.35e-14 EndAngle=1.5708
    g7: LineSegment StartX=10.0875 StartY=-1.11588 StartZ=0 EndX=10.0875 EndY=1.38411 EndZ=0
    g8: ArcOfCircle CenterX=7.08745 CenterY=1.38411 CenterZ=0 NormalX=0 NormalY=0 NormalZ=1 AngleXU=0 Radius=3 StartAngle=3.57e-14 EndAngle=1.5708
    g9: ArcOfCircle CenterX=4.58745 CenterY=1.38412 CenterZ=0 NormalX=0 NormalY=0 NormalZ=1 AngleXU=0 Radius=1 StartAngle=1.57081 EndAngle=3.14159
    g10: LineSegment StartX=4.58744 StartY=2.38411 StartZ=0 EndX=7.08745 EndY=2.38411 EndZ=0
    g11: LineSegment StartX=4.58745 StartY=4.38411 StartZ=0 EndX=7.08745 EndY=4.38411 EndZ=0
    g12: ArcOfCircle CenterX=4.58745 CenterY=5.38411 CenterZ=0 NormalX=0 NormalY=0 NormalZ=1 AngleXU=0 Radius=1 StartAngle=3.14159 EndAngle=4.71239
    g13: LineSegment StartX=3.58745 StartY=5.38411 StartZ=0 EndX=3.58745 EndY=1.38411 EndZ=0
  constraints (33):
    c: Vertical(g0)
    c: Block(g0)
    c: Block(g1)
    c: Coincident(g2,g1)
    c: Coincident(g3,g0)
    c: Coincident(g3,g2)
    c: Horizontal(g3)
    c: Block(g2)
    c: Coincident(g4,g0)
    c: Horizontal(g4)
    c: Coincident(g5,g2)
    c: Block(g5)
    c: Block(g4)
    c: Coincident(g6,g1)
    c: Block(g6)
    c: Coincident(g7,g5)
    c: Vertical(g7)
    c: Coincident(g8,g6)
    c: Block(g8)
    c: Block(g7)
    c: Coincident(g10,g9)
    c: Coincident(g10,g6)
    c: Horizontal(g10)
    c: Block(g10)
    c: Block(g9)
    c: Coincident(g11,g8)
    c: Horizontal(g11)
    c: Block(g12)
    c: Block(g11)
    c: Coincident(g13,g12)
    c: Coincident(g13,g9)
    c: Vertical(g13)
    c: Tangent(g13,g9)
FEATURE [Part::Extrusion] Extrude040
  Base = -> Sketch045
  Dir = (1,0,0)
  DirMode = 2
  FaceMakerClass = Part::FaceMakerBullseye
  LengthFwd = 10
  LengthRev = 0
  Placement = pos=(-17.5,-22.615,4.115) rot=(0,0,1;3.14159rad)
  Solid = true
  Symmetric = false
FEATURE [Sketcher::SketchObject] Sketch046
  FullyConstrained = true
  MapMode = 4
  Placement = pos=(0,0,0) rot=(0.57735,0.57735,0.57735;2.0944rad)
  Support = -> [Cut014]
  sketch-geometry (14):
    g0: LineSegment StartX=6.08745 StartY=-4.11588 StartZ=0 EndX=6.08745 EndY=-2.11589 EndZ=0
    g1: LineSegment StartX=8.08745 StartY=1.38411 StartZ=0 EndX=8.08745 EndY=-1.11589 EndZ=0
    g2: ArcOfCircle CenterX=7.08745 CenterY=-1.11589 CenterZ=0 NormalX=0 NormalY=0 NormalZ=1 AngleXU=0 Radius=1 StartAngle=4.71239 EndAngle=6.28319
    g3: LineSegment StartX=6.08745 StartY=-2.11589 StartZ=0 EndX=7.08745 EndY=-2.11589 EndZ=0
    g4: LineSegment StartX=6.08745 StartY=-4.11588 StartZ=0 EndX=7.08745 EndY=-4.11588 EndZ=0
    g5: ArcOfCircle CenterX=7.08745 CenterY=-1.11589 CenterZ=0 NormalX=0 NormalY=0 NormalZ=1 AngleXU=0 Radius=3 StartAngle=4.71239 EndAngle=6.28319
    g6: ArcOfCircle CenterX=7.08745 CenterY=1.38411 CenterZ=0 NormalX=0 NormalY=0 NormalZ=1 AngleXU=0 Radius=1 StartAngle=5.35e-14 EndAngle=1.5708
    g7: LineSegment StartX=10.0875 StartY=-1.11588 StartZ=0 EndX=10.0875 EndY=1.38411 EndZ=0
    g8: ArcOfCircle CenterX=7.08745 CenterY=1.38411 CenterZ=0 NormalX=0 NormalY=0 NormalZ=1 AngleXU=0 Radius=3 StartAngle=3.57e-14 EndAngle=1.5708
    g9: ArcOfCircle CenterX=4.58745 CenterY=1.38412 CenterZ=0 NormalX=0 NormalY=0 NormalZ=1 AngleXU=0 Radius=1 StartAngle=1.57081 EndAngle=3.14159
    g10: LineSegment StartX=4.58744 StartY=2.38411 StartZ=0 EndX=7.08745 EndY=2.38411 EndZ=0
    g11: LineSegment StartX=4.58745 StartY=4.38411 StartZ=0 EndX=7.08745 EndY=4.38411 EndZ=0
    g12: ArcOfCircle CenterX=4.58745 CenterY=5.38411 CenterZ=0 NormalX=0 NormalY=0 NormalZ=1 AngleXU=0 Radius=1 StartAngle=3.14159 EndAngle=4.71239
    g13: LineSegment StartX=3.58745 StartY=5.38411 StartZ=0 EndX=3.58745 EndY=1.38411 EndZ=0
  constraints (33):
    c: Vertical(g0)
    c: Block(g0)
    c: Block(g1)
    c: Coincident(g2,g1)
    c: Coincident(g3,g0)
    c: Coincident(g3,g2)
    c: Horizontal(g3)
    c: Block(g2)
    c: Coincident(g4,g0)
    c: Horizontal(g4)
    c: Coincident(g5,g2)
    c: Block(g5)
    c: Block(g4)
    c: Coincident(g6,g1)
    c: Block(g6)
    c: Coincident(g7,g5)
    c: Vertical(g7)
    c: Coincident(g8,g6)
    c: Block(g8)
    c: Block(g7)
    c: Coincident(g10,g9)
    c: Coincident(g10,g6)
    c: Horizontal(g10)
    c: Block(g10)
    c: Block(g9)
    c: Coincident(g11,g8)
    c: Horizontal(g11)
    c: Block(g12)
    c: Block(g11)
    c: Coincident(g13,g12)
    c: Coincident(g13,g9)
    c: Vertical(g13)
    c: Tangent(g13,g9)
FEATURE [Sketcher::SketchObject] Sketch047
  FullyConstrained = true
  MapMode = 4
  Placement = pos=(0,0,0) rot=(0.57735,0.57735,0.57735;2.0944rad)
  Support = -> [Cut014]
  sketch-geometry (14):
    g0: LineSegment StartX=6.08745 StartY=-4.11588 StartZ=0 EndX=6.08745 EndY=-2.11589 EndZ=0
    g1: LineSegment StartX=8.08745 StartY=1.38411 StartZ=0 EndX=8.08745 EndY=-1.11589 EndZ=0
    g2: ArcOfCircle CenterX=7.08745 CenterY=-1.11589 CenterZ=0 NormalX=0 NormalY=0 NormalZ=1 AngleXU=0 Radius=1 StartAngle=4.71239 EndAngle=6.28319
    g3: LineSegment StartX=6.08745 StartY=-2.11589 StartZ=0 EndX=7.08745 EndY=-2.11589 EndZ=0
    g4: LineSegment StartX=6.08745 StartY=-4.11588 StartZ=0 EndX=7.08745 EndY=-4.11588 EndZ=0
    g5: ArcOfCircle CenterX=7.08745 CenterY=-1.11589 CenterZ=0 NormalX=0 NormalY=0 NormalZ=1 AngleXU=0 Radius=3 StartAngle=4.71239 EndAngle=6.28319
    g6: ArcOfCircle CenterX=7.08745 CenterY=1.38411 CenterZ=0 NormalX=0 NormalY=0 NormalZ=1 AngleXU=0 Radius=1 StartAngle=5.35e-14 EndAngle=1.5708
    g7: LineSegment StartX=10.0875 StartY=-1.11588 StartZ=0 EndX=10.0875 EndY=1.38411 EndZ=0
    g8: ArcOfCircle CenterX=7.08745 CenterY=1.38411 CenterZ=0 NormalX=0 NormalY=0 NormalZ=1 AngleXU=0 Radius=3 StartAngle=3.57e-14 EndAngle=1.5708
    g9: ArcOfCircle CenterX=4.58745 CenterY=1.38412 CenterZ=0 NormalX=0 NormalY=0 NormalZ=1 AngleXU=0 Radius=1 StartAngle=1.57081 EndAngle=3.14159
    g10: LineSegment StartX=4.58744 StartY=2.38411 StartZ=0 EndX=7.08745 EndY=2.38411 EndZ=0
    g11: LineSegment StartX=4.58745 StartY=4.38411 StartZ=0 EndX=7.08745 EndY=4.38411 EndZ=0
    g12: ArcOfCircle CenterX=4.58745 CenterY=5.38411 CenterZ=0 NormalX=0 NormalY=0 NormalZ=1 AngleXU=0 Radius=1 StartAngle=3.14159 EndAngle=4.71239
    g13: LineSegment StartX=3.58745 StartY=5.38411 StartZ=0 EndX=3.58745 EndY=1.38411 EndZ=0
  constraints (33):
    c: Vertical(g0)
    c: Block(g0)
    c: Block(g1)
    c: Coincident(g2,g1)
    c: Coincident(g3,g0)
    c: Coincident(g3,g2)
    c: Horizontal(g3)
    c: Block(g2)
    c: Coincident(g4,g0)
    c: Horizontal(g4)
    c: Coincident(g5,g2)
    c: Block(g5)
    c: Block(g4)
    c: Coincident(g6,g1)
    c: Block(g6)
    c: Coincident(g7,g5)
    c: Vertical(g7)
    c: Coincident(g8,g6)
    c: Block(g8)
    c: Block(g7)
    c: Coincident(g10,g9)
    c: Coincident(g10,g6)
    c: Horizontal(g10)
    c: Block(g10)
    c: Block(g9)
    c: Coincident(g11,g8)
    c: Horizontal(g11)
    c: Block(g12)
    c: Block(g11)
    c: Coincident(g13,g12)
    c: Coincident(g13,g9)
    c: Vertical(g13)
    c: Tangent(g13,g9)
FEATURE [Sketcher::SketchObject] Sketch048
  FullyConstrained = true
  MapMode = 4
  Placement = pos=(0,0,0) rot=(0.57735,0.57735,0.57735;2.0944rad)
  Support = -> [Cut014]
  sketch-geometry (14):
    g0: LineSegment StartX=6.08745 StartY=-4.11588 StartZ=0 EndX=6.08745 EndY=-2.11589 EndZ=0
    g1: LineSegment StartX=8.08745 StartY=1.38411 StartZ=0 EndX=8.08745 EndY=-1.11589 EndZ=0
    g2: ArcOfCircle CenterX=7.08745 CenterY=-1.11589 CenterZ=0 NormalX=0 NormalY=0 NormalZ=1 AngleXU=0 Radius=1 StartAngle=4.71239 EndAngle=6.28319
    g3: LineSegment StartX=6.08745 StartY=-2.11589 StartZ=0 EndX=7.08745 EndY=-2.11589 EndZ=0
    g4: LineSegment StartX=6.08745 StartY=-4.11588 StartZ=0 EndX=7.08745 EndY=-4.11588 EndZ=0
    g5: ArcOfCircle CenterX=7.08745 CenterY=-1.11589 CenterZ=0 NormalX=0 NormalY=0 NormalZ=1 AngleXU=0 Radius=3 StartAngle=4.71239 EndAngle=6.28319
    g6: ArcOfCircle CenterX=7.08745 CenterY=1.38411 CenterZ=0 NormalX=0 NormalY=0 NormalZ=1 AngleXU=0 Radius=1 StartAngle=5.35e-14 EndAngle=1.5708
    g7: LineSegment StartX=10.0875 StartY=-1.11588 StartZ=0 EndX=10.0875 EndY=1.38411 EndZ=0
    g8: ArcOfCircle CenterX=7.08745 CenterY=1.38411 CenterZ=0 NormalX=0 NormalY=0 NormalZ=1 AngleXU=0 Radius=3 StartAngle=3.57e-14 EndAngle=1.5708
    g9: ArcOfCircle CenterX=4.58745 CenterY=1.38412 CenterZ=0 NormalX=0 NormalY=0 NormalZ=1 AngleXU=0 Radius=1 StartAngle=1.57081 EndAngle=3.14159
    g10: LineSegment StartX=4.58744 StartY=2.38411 StartZ=0 EndX=7.08745 EndY=2.38411 EndZ=0
    g11: LineSegment StartX=4.58745 StartY=4.38411 StartZ=0 EndX=7.08745 EndY=4.38411 EndZ=0
    g12: ArcOfCircle CenterX=4.58745 CenterY=5.38411 CenterZ=0 NormalX=0 NormalY=0 NormalZ=1 AngleXU=0 Radius=1 StartAngle=3.14159 EndAngle=4.71239
    g13: LineSegment StartX=3.58745 StartY=5.38411 StartZ=0 EndX=3.58745 EndY=1.38411 EndZ=0
  constraints (33):
    c: Vertical(g0)
    c: Block(g0)
    c: Block(g1)
    c: Coincident(g2,g1)
    c: Coincident(g3,g0)
    c: Coincident(g3,g2)
    c: Horizontal(g3)
    c: Block(g2)
    c: Coincident(g4,g0)
    c: Horizontal(g4)
    c: Coincident(g5,g2)
    c: Block(g5)
    c: Block(g4)
    c: Coincident(g6,g1)
    c: Block(g6)
    c: Coincident(g7,g5)
    c: Vertical(g7)
    c: Coincident(g8,g6)
    c: Block(g8)
    c: Block(g7)
    c: Coincident(g10,g9)
    c: Coincident(g10,g6)
    c: Horizontal(g10)
    c: Block(g10)
    c: Block(g9)
    c: Coincident(g11,g8)
    c: Horizontal(g11)
    c: Block(g12)
    c: Block(g11)
    c: Coincident(g13,g12)
    c: Coincident(g13,g9)
    c: Vertical(g13)
    c: Tangent(g13,g9)
FEATURE [Sketcher::SketchObject] Sketch049
  FullyConstrained = true
  MapMode = 4
  Placement = pos=(0,0,0) rot=(0.57735,0.57735,0.57735;2.0944rad)
  Support = -> [Cut014]
  sketch-geometry (14):
    g0: LineSegment StartX=6.08745 StartY=-4.11588 StartZ=0 EndX=6.08745 EndY=-2.11589 EndZ=0
    g1: LineSegment StartX=8.08745 StartY=1.38411 StartZ=0 EndX=8.08745 EndY=-1.11589 EndZ=0
    g2: ArcOfCircle CenterX=7.08745 CenterY=-1.11589 CenterZ=0 NormalX=0 NormalY=0 NormalZ=1 AngleXU=0 Radius=1 StartAngle=4.71239 EndAngle=6.28319
    g3: LineSegment StartX=6.08745 StartY=-2.11589 StartZ=0 EndX=7.08745 EndY=-2.11589 EndZ=0
    g4: LineSegment StartX=6.08745 StartY=-4.11588 StartZ=0 EndX=7.08745 EndY=-4.11588 EndZ=0
    g5: ArcOfCircle CenterX=7.08745 CenterY=-1.11589 CenterZ=0 NormalX=0 NormalY=0 NormalZ=1 AngleXU=0 Radius=3 StartAngle=4.71239 EndAngle=6.28319
    g6: ArcOfCircle CenterX=7.08745 CenterY=1.38411 CenterZ=0 NormalX=0 NormalY=0 NormalZ=1 AngleXU=0 Radius=1 StartAngle=5.35e-14 EndAngle=1.5708
    g7: LineSegment StartX=10.0875 StartY=-1.11588 StartZ=0 EndX=10.0875 EndY=1.38411 EndZ=0
    g8: ArcOfCircle CenterX=7.08745 CenterY=1.38411 CenterZ=0 NormalX=0 NormalY=0 NormalZ=1 AngleXU=0 Radius=3 StartAngle=3.57e-14 EndAngle=1.5708
    g9: ArcOfCircle CenterX=4.58745 CenterY=1.38412 CenterZ=0 NormalX=0 NormalY=0 NormalZ=1 AngleXU=0 Radius=1 StartAngle=1.57081 EndAngle=3.14159
    g10: LineSegment StartX=4.58744 StartY=2.38411 StartZ=0 EndX=7.08745 EndY=2.38411 EndZ=0
    g11: LineSegment StartX=4.58745 StartY=4.38411 StartZ=0 EndX=7.08745 EndY=4.38411 EndZ=0
    g12: ArcOfCircle CenterX=4.58745 CenterY=5.38411 CenterZ=0 NormalX=0 NormalY=0 NormalZ=1 AngleXU=0 Radius=1 StartAngle=3.14159 EndAngle=4.71239
    g13: LineSegment StartX=3.58745 StartY=5.38411 StartZ=0 EndX=3.58745 EndY=1.38411 EndZ=0
  constraints (33):
    c: Vertical(g0)
    c: Block(g0)
    c: Block(g1)
    c: Coincident(g2,g1)
    c: Coincident(g3,g0)
    c: Coincident(g3,g2)
    c: Horizontal(g3)
    c: Block(g2)
    c: Coincident(g4,g0)
    c: Horizontal(g4)
    c: Coincident(g5,g2)
    c: Block(g5)
    c: Block(g4)
    c: Coincident(g6,g1)
    c: Block(g6)
    c: Coincident(g7,g5)
    c: Vertical(g7)
    c: Coincident(g8,g6)
    c: Block(g8)
    c: Block(g7)
    c: Coincident(g10,g9)
    c: Coincident(g10,g6)
    c: Horizontal(g10)
    c: Block(g10)
    c: Block(g9)
    c: Coincident(g11,g8)
    c: Horizontal(g11)
    c: Block(g12)
    c: Block(g11)
    c: Coincident(g13,g12)
    c: Coincident(g13,g9)
    c: Vertical(g13)
    c: Tangent(g13,g9)
FEATURE [Part::Extrusion] Extrude041
  Base = -> Sketch049
  Dir = (1,0,0)
  DirMode = 2
  FaceMakerClass = Part::FaceMakerBullseye
  LengthFwd = 10
  LengthRev = 0
  Placement = pos=(-2,-22.615,14.6) rot=(0,0,1;3.14159rad)
  Solid = true
  Symmetric = false
FEATURE [Part::MultiFuse] Fusion023
  Shapes = -> [Extrude039,Extrude040,Extrude041,Cut014,Fusion015]
FEATURE [Part::Extrusion] Extrude042
  Base = -> Sketch034
  Dir = (0,0.894389,-0.447291)
  DirMode = 2
  FaceMakerClass = Part::FaceMakerBullseye
  LengthFwd = 14
  LengthRev = 0
  Placement = pos=(45.5,-14,11) rot=(1,0,0;0.466003rad)
  Solid = true
  Symmetric = false
FEATURE [Part::Fillet] Fillet021
  Base = -> Extrude042
  Edges = 1 edges r=1.95: [Edge2]
FEATURE [Part::Fillet] Fillet022
  Base = -> Fillet021
  Edges = 1 edges r=1.9: [Edge12]
